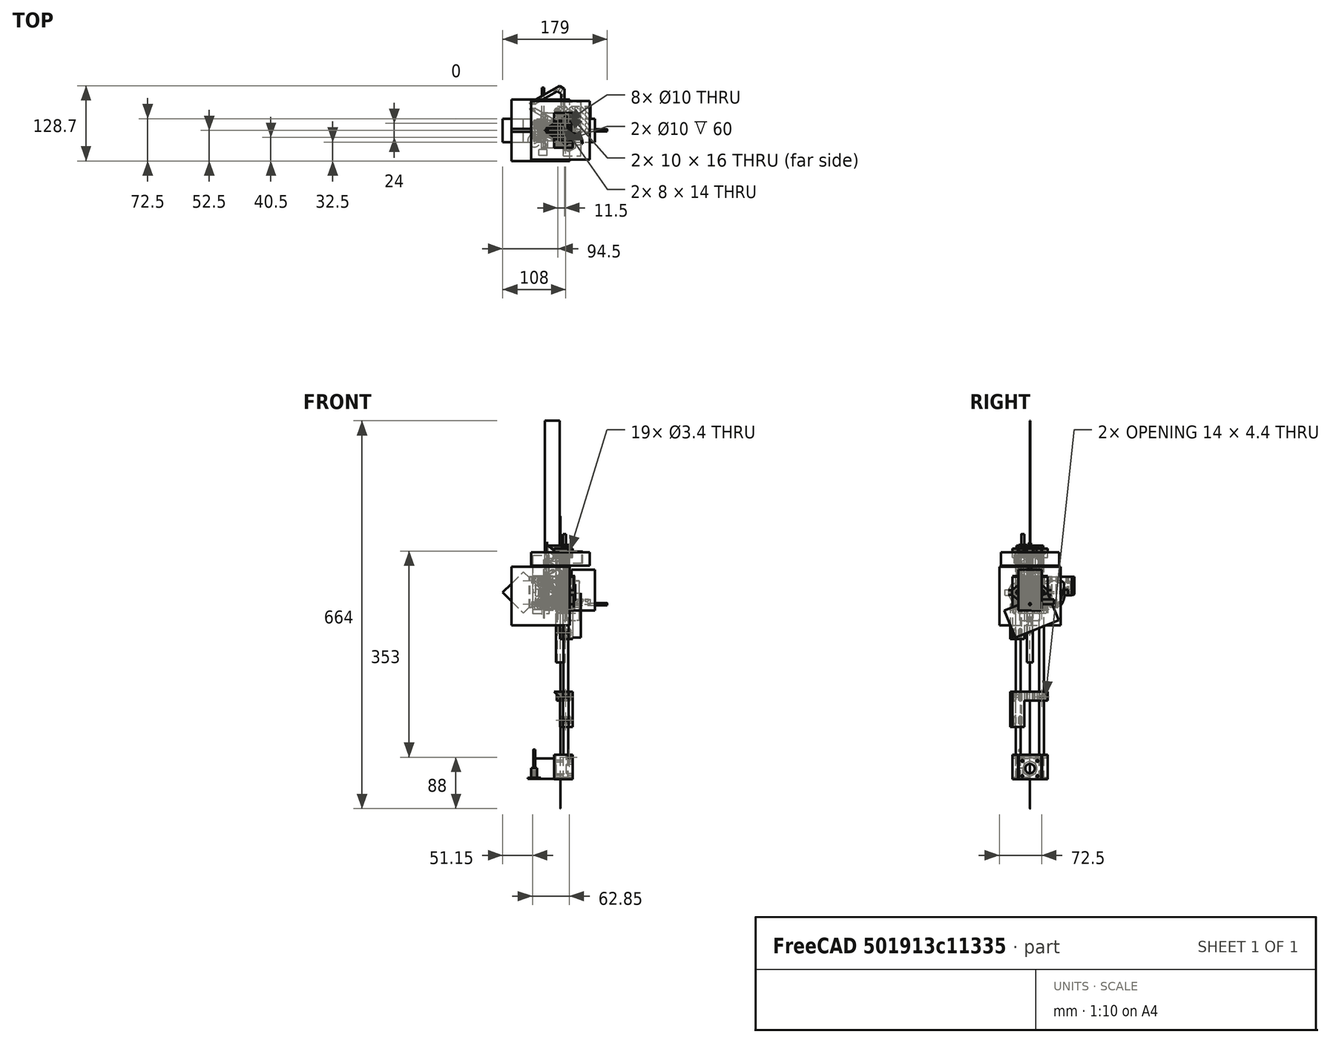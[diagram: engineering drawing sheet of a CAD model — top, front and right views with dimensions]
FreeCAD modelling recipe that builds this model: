
FCSTD DOCUMENT  (FreeCAD 0.16R6703 (Git))
Label: lorenz
License: All rights reserved
LicenseURL: http://en.wikipedia.org/wiki/All_rights_reserved
objects: Part::Cut×262, Part::Box×156, Part::Feature×140, Part::Cylinder×109, Part::Fuse×108, Part::Chamfer×36, Part::MultiCommon×15, Part::Mirroring×10, Part::Cone×10, Part::Sphere×9, App::DocumentObjectGroup×6, Part::Fillet×5
note: 860 computed .brp shape members not serialized (recipe doc carries the construction recipe); baked Part::Feature solids carry a one-line shape summary decoded from their .brp

FEATURE [Part::Box] Box  label="rule"
  Height = 324
  Length = 25.5
  Placement = pos=(-27,-0.33,-10) rot=(0,0,1;0rad)
  Width = 0.66
FEATURE [Part::Cylinder] Cylinder  label="threadrunner1"
  Angle = 360
  Height = 6
  Placement = pos=(-32,3,0) rot=(1,0,0;1.5708rad)
  Radius = 6.5
FEATURE [Part::Cylinder] Cylinder001  label="threadRunner2"
  Angle = 360
  Height = 6
  Placement = pos=(-32,3,40) rot=(1,0,0;1.5708rad)
  Radius = 6.5
FEATURE [Part::Box] Box001  label="Cube"
  Height = 110
  Length = 40
  Placement = pos=(15,-30,-5) rot=(0,0,1;0rad)
  Width = 60
FEATURE [Part::Cylinder] Cylinder002  label="Cylinder"
  Angle = 360
  Height = 100
  Radius = 34
FEATURE [Part::Feature] Box002
  Placement = pos=(18.4808,27.9904,-5) rot=(0,0,1;2.0944rad)
  shape: bbox 71.96 x 64.64 x 110 mm, 6 faces (baked)
FEATURE [Part::Feature] Box003
  Placement = pos=(-33.4808,2.00962,-5) rot=(0,0,1;4.18879rad)
  shape: bbox 71.96 x 64.64 x 110 mm, 6 faces (baked)
FEATURE [Part::Box] Box004  label="Cube001"
  Height = 110
  Length = 40
  Placement = pos=(10,-30,-5) rot=(0,0,1;0rad)
  Width = 60
FEATURE [Part::Feature] Box005
  Placement = pos=(20.9808,23.6603,-5) rot=(0,0,1;2.0944rad)
  shape: bbox 71.96 x 64.64 x 110 mm, 6 faces (baked)
FEATURE [Part::Feature] Box006
  Placement = pos=(-30.9808,6.33975,-5) rot=(0,0,1;4.18879rad)
  shape: bbox 71.96 x 64.64 x 110 mm, 6 faces (baked)
FEATURE [Part::Cylinder] Cylinder003  label="Cylinder001"
  Angle = 360
  Height = 102
  Placement = pos=(0,0,-1) rot=(0,0,1;0rad)
  Radius = 34
FEATURE [Part::Cut] Cut
  Base = -> Cylinder002
  Tool = -> Box001
FEATURE [Part::Cut] Cut001
  Base = -> Cut
  Tool = -> Box002
FEATURE [Part::Cut] Cut002
  Base = -> Cut001
  Tool = -> Box003
FEATURE [Part::Cut] Cut003
  Base = -> Cylinder003
  Tool = -> Box004
FEATURE [Part::Cut] Cut004
  Base = -> Cut003
  Tool = -> Box006
FEATURE [Part::Cut] Cut005
  Base = -> Cut004
  Tool = -> Box005
FEATURE [Part::Cut] Cut006
  Base = -> Cut002
  Tool = -> Cut005
FEATURE [Part::Box] Box007  label="Cube002"
  Height = 110
  Length = 40
  Placement = pos=(40.4808,4.99038,-5) rot=(0,0,1;1.0472rad)
  Width = 60
FEATURE [Part::Feature] Box008
  Placement = pos=(-24.5622,32.5622,-5) rot=(0,0,1;3.14159rad)
  shape: bbox 40 x 60 x 110 mm, 6 faces (baked)
FEATURE [Part::Feature] Box009
  Placement = pos=(-15.9186,-37.5526,-5) rot=(0,0,-1;1.0472rad)
  shape: bbox 71.96 x 64.64 x 110 mm, 6 faces (baked)
FEATURE [Part::Cut] Cut007
  Base = -> Cut006
  Tool = -> Box007
FEATURE [Part::Cut] Cut008
  Base = -> Cut007
  Tool = -> Box008
FEATURE [Part::Cut] Cut009
  Base = -> Cut008
  Tool = -> Box009
FEATURE [Part::Box] Box010  label="Cube003"
  Height = 100
  Length = 37
  Placement = pos=(-22,-4,0) rot=(0,0,1;0rad)
  Width = 8
FEATURE [Part::Box] Box011  label="Cube004"
  Height = 110
  Length = 40
  Placement = pos=(10,-30,-5) rot=(0,0,1;0rad)
  Width = 60
FEATURE [Part::Feature] Box012
  Placement = pos=(20.9808,23.6603,-5) rot=(0,0,1;2.0944rad)
  shape: bbox 71.96 x 64.64 x 110 mm, 6 faces (baked)
FEATURE [Part::Feature] Box013
  Placement = pos=(-30.9808,6.33975,-5) rot=(0,0,1;4.18879rad)
  shape: bbox 71.96 x 64.64 x 110 mm, 6 faces (baked)
FEATURE [Part::Cylinder] Cylinder004  label="Cylinder002"
  Angle = 360
  Height = 102
  Placement = pos=(0,0,-1) rot=(0,0,1;0rad)
  Radius = 34
FEATURE [Part::Cut] Cut010
  Base = -> Cylinder004
  Tool = -> Box011
FEATURE [Part::Cut] Cut011
  Base = -> Cut010
  Tool = -> Box013
FEATURE [Part::Cut] Cut012
  Base = -> Cut011
  Placement = pos=(111,-4.5,71.8801) rot=(-0.250563,-0.935113,0.250563;1.63783rad)
  Tool = -> Box012
FEATURE [Part::Box] Box014  label="Cube005"
  Height = 110
  Length = 40
  Placement = pos=(10,-30,-5) rot=(0,0,1;0rad)
  Width = 60
FEATURE [Part::Feature] Box015
  Placement = pos=(20.9808,23.6603,-5) rot=(0,0,1;2.0944rad)
  shape: bbox 71.96 x 64.64 x 110 mm, 6 faces (baked)
FEATURE [Part::Feature] Box016
  Placement = pos=(-30.9808,6.33975,-5) rot=(0,0,1;4.18879rad)
  shape: bbox 71.96 x 64.64 x 110 mm, 6 faces (baked)
FEATURE [Part::Cylinder] Cylinder005  label="Cylinder003"
  Angle = 360
  Height = 102
  Placement = pos=(0,0,-1) rot=(0,0,1;0rad)
  Radius = 34
FEATURE [Part::Cut] Cut013
  Base = -> Cylinder005
  Tool = -> Box014
FEATURE [Part::Cut] Cut014
  Base = -> Cut013
  Tool = -> Box016
FEATURE [Part::Cut] Cut015
  Base = -> Cut014
  Placement = pos=(111,-4.5,71.8801) rot=(-0.250563,-0.935113,0.250563;1.63783rad)
  Tool = -> Box015
FEATURE [Part::Box] Box017  label="Cube006"
  Height = 29
  Length = 120
  Placement = pos=(0,-18,43) rot=(0,0,1;0rad)
  Width = 36
FEATURE [Part::Box] Box018  label="Cube007"
  Height = 29
  Length = 120
  Placement = pos=(0,-18,43) rot=(0,0,1;0rad)
  Width = 36
FEATURE [Part::Cut] Cut016
  Base = -> Cut012
  Placement = pos=(0,0,-67) rot=(0,0,1;0rad)
  Tool = -> Box017
FEATURE [Part::MultiCommon] Common
  Placement = pos=(8,0,24) rot=(0,0,1;0rad)
  Shapes = -> [Cut015,Box018]
FEATURE [Part::Box] Box019  label="Cube008"
  Height = 110
  Length = 40
  Placement = pos=(10,-30,-5) rot=(0,0,1;0rad)
  Width = 60
FEATURE [Part::Feature] Box020
  Placement = pos=(20.9808,23.6603,-5) rot=(0,0,1;2.0944rad)
  shape: bbox 71.96 x 64.64 x 110 mm, 6 faces (baked)
FEATURE [Part::Feature] Box021
  Placement = pos=(-30.9808,6.33975,-5) rot=(0,0,1;4.18879rad)
  shape: bbox 71.96 x 64.64 x 110 mm, 6 faces (baked)
FEATURE [Part::Cylinder] Cylinder006  label="Cylinder004"
  Angle = 360
  Height = 102
  Placement = pos=(0,0,-1) rot=(0,0,1;0rad)
  Radius = 34
FEATURE [Part::Cut] Cut017
  Base = -> Cylinder006
  Tool = -> Box019
FEATURE [Part::Cut] Cut018
  Base = -> Cut017
  Tool = -> Box021
FEATURE [Part::Cut] Cut019
  Base = -> Cut018
  Placement = pos=(111,4.93525,72.5429) rot=(0.250562,-0.935113,-0.250563;1.63783rad)
  Tool = -> Box020
FEATURE [Part::Box] Box022  label="Cube009"
  Height = 110
  Length = 40
  Placement = pos=(10,-30,-5) rot=(0,0,1;0rad)
  Width = 60
FEATURE [Part::Feature] Box023
  Placement = pos=(20.9808,23.6603,-5) rot=(0,0,1;2.0944rad)
  shape: bbox 71.96 x 64.64 x 110 mm, 6 faces (baked)
FEATURE [Part::Feature] Box024
  Placement = pos=(-30.9808,6.33975,-5) rot=(0,0,1;4.18879rad)
  shape: bbox 71.96 x 64.64 x 110 mm, 6 faces (baked)
FEATURE [Part::Cylinder] Cylinder007  label="Cylinder005"
  Angle = 360
  Height = 102
  Placement = pos=(0,0,-1) rot=(0,0,1;0rad)
  Radius = 34
FEATURE [Part::Cut] Cut020
  Base = -> Cylinder007
  Tool = -> Box022
FEATURE [Part::Cut] Cut021
  Base = -> Cut020
  Tool = -> Box024
FEATURE [Part::Cut] Cut022
  Base = -> Cut021
  Placement = pos=(111,-4.84232,50.4974) rot=(-0.250563,-0.935113,0.250563;1.63783rad)
  Tool = -> Box023
FEATURE [Part::Box] Box025  label="Cube010"
  Height = 110
  Length = 40
  Placement = pos=(10,-30,-5) rot=(0,0,1;0rad)
  Width = 60
FEATURE [Part::Feature] Box026
  Placement = pos=(20.9808,23.6603,-5) rot=(0,0,1;2.0944rad)
  shape: bbox 71.96 x 64.64 x 110 mm, 6 faces (baked)
FEATURE [Part::Feature] Box027
  Placement = pos=(-30.9808,6.33975,-5) rot=(0,0,1;4.18879rad)
  shape: bbox 71.96 x 64.64 x 110 mm, 6 faces (baked)
FEATURE [Part::Cylinder] Cylinder008  label="Cylinder006"
  Angle = 360
  Height = 102
  Placement = pos=(0,0,-1) rot=(0,0,1;0rad)
  Radius = 34
FEATURE [Part::Cut] Cut023
  Base = -> Cylinder008
  Tool = -> Box025
FEATURE [Part::Cut] Cut024
  Base = -> Cut023
  Tool = -> Box027
FEATURE [Part::Cut] Cut025
  Base = -> Cut024
  Placement = pos=(111,4.93525,28.5429) rot=(0.250562,-0.935113,-0.250563;1.63783rad)
  Tool = -> Box026
FEATURE [Part::Fuse] Fusion
  Base = -> Cut016
  Tool = -> Cut025
FEATURE [Part::Fuse] Fusion001
  Base = -> Cut022
  Tool = -> Fusion
FEATURE [Part::Fuse] Fusion002
  Base = -> Cut019
  Tool = -> Fusion001
FEATURE [Part::Fuse] Fusion003
  Base = -> Common
  Placement = pos=(-1,0,0) rot=(0,0,1;0rad)
  Tool = -> Fusion002
FEATURE [Part::Feature] Fusion004
  Placement = pos=(0.5,-0.866025,0) rot=(0,0,1;2.0944rad)
  shape: bbox 77.47 x 103.6 x 91 mm, 26 faces, 5 solids (baked)
FEATURE [Part::Feature] Fusion005
  Placement = pos=(0.5,0.866025,0) rot=(0,0,1;4.18879rad)
  shape: bbox 77.47 x 103.6 x 91 mm, 26 faces, 5 solids (baked)
FEATURE [Part::Cut] Cut026
  Base = -> Cut009
  Tool = -> Fusion003
FEATURE [Part::Cut] Cut027
  Base = -> Cut026
  Tool = -> Fusion004
FEATURE [Part::Cut] Cut028
  Base = -> Cut027
  Tool = -> Fusion005
FEATURE [Part::Fuse] Fusion006
  Base = -> Box010
  Tool = -> Cut028
FEATURE [Part::Box] Box028  label="rule001"
  Height = 324
  Length = 26.5
  Placement = pos=(-27,-0.45,-10) rot=(0,0,1;0rad)
  Width = 0.9
FEATURE [Part::Cut] Cut029  label="stator"
  Base = -> Fusion006
  Tool = -> Box028
FEATURE [Part::Cylinder] Cylinder012
  Angle = 360
  Height = 54
  Placement = pos=(0,0,-7) rot=(0,0,1;0rad)
  Radius = 31
FEATURE [Part::Box] Box029  label="Cube011"
  Height = 60
  Length = 50
  Placement = pos=(21,-25,-10) rot=(0,0,1;0rad)
  Width = 50
FEATURE [Part::Feature] Box030
  Placement = pos=(11.1506,30.6865,-10) rot=(0,0,1;2.0944rad)
  shape: bbox 68.3 x 68.3 x 60 mm, 6 faces (baked)
FEATURE [Part::Feature] Box031
  Placement = pos=(-32.1506,-5.68653,-10) rot=(0,0,1;4.18879rad)
  shape: bbox 68.3 x 68.3 x 60 mm, 6 faces (baked)
FEATURE [Part::Cut] Cut030
  Base = -> Cylinder012
  Tool = -> Box029
FEATURE [Part::Cut] Cut031
  Base = -> Cut030
  Tool = -> Box031
FEATURE [Part::Cut] Cut032
  Base = -> Cut031
  Tool = -> Box030
FEATURE [Part::Box] Box032  label="Cube012"
  Height = 60
  Length = 50
  Placement = pos=(16,-30,-10) rot=(0,0,1;0rad)
  Width = 60
FEATURE [Part::Cylinder] Cylinder013
  Angle = 360
  Height = 56
  Placement = pos=(0,0,-8) rot=(0,0,1;0rad)
  Radius = 31
FEATURE [Part::Feature] Box033
  Placement = pos=(17.9808,28.8564,-10) rot=(0,0,1;2.0944rad)
  shape: bbox 76.96 x 73.3 x 60 mm, 6 faces (baked)
FEATURE [Part::Feature] Box034
  Placement = pos=(-33.9808,1.14359,-10) rot=(0,0,1;4.18879rad)
  shape: bbox 76.96 x 73.3 x 60 mm, 6 faces (baked)
FEATURE [Part::Box] Box035  label="Cube013"
  Height = 60
  Length = 50
  Placement = pos=(-76,-30,-10) rot=(0,0,1;0rad)
  Width = 60
FEATURE [Part::Feature] Box036
  Placement = pos=(63.9808,-50.8179,-10) rot=(0,0,1;2.0944rad)
  shape: bbox 76.96 x 73.3 x 60 mm, 6 faces (baked)
FEATURE [Part::Feature] Box037
  Placement = pos=(12.0192,80.8179,-10) rot=(0,0,1;4.18879rad)
  shape: bbox 76.96 x 73.3 x 60 mm, 6 faces (baked)
FEATURE [Part::Cut] Cut033
  Base = -> Cylinder013
  Tool = -> Box032
FEATURE [Part::Cut] Cut034
  Base = -> Cut033
  Tool = -> Box037
FEATURE [Part::Cut] Cut035
  Base = -> Cut034
  Tool = -> Box036
FEATURE [Part::Cut] Cut036
  Base = -> Cut035
  Tool = -> Box035
FEATURE [Part::Cut] Cut037
  Base = -> Cut036
  Tool = -> Box034
FEATURE [Part::Cut] Cut038
  Base = -> Cut037
  Tool = -> Box033
FEATURE [Part::Cut] Cut039
  Base = -> Cut032
  Tool = -> Cut038
FEATURE [Part::Box] Box038  label="rule002"
  Height = 324
  Length = 26.5
  Placement = pos=(-29,-1.5,-10) rot=(0,0,1;0rad)
  Width = 3
FEATURE [Part::Box] Box039  label="Cube014"
  Height = 15
  Length = 12
  Placement = pos=(-39,-9,-7) rot=(0,0,1;0rad)
  Width = 18
FEATURE [Part::Box] Box040  label="Cube015"
  Height = 15
  Length = 27
  Placement = pos=(-44,-4,-7) rot=(0,0,1;0rad)
  Width = 8
FEATURE [Part::Box] Box041  label="Cube016"
  Height = 15
  Length = 12
  Placement = pos=(-39,-9,32) rot=(0,0,1;0rad)
  Width = 18
FEATURE [Part::Box] Box042  label="Cube017"
  Height = 15
  Length = 27
  Placement = pos=(-44,-4,32) rot=(0,0,1;0rad)
  Width = 8
FEATURE [Part::Fuse] Fusion007
  Base = -> Cut039
  Tool = -> Box039
FEATURE [Part::Fuse] Fusion008
  Base = -> Box041
  Tool = -> Fusion007
FEATURE [Part::Cut] Cut040
  Base = -> Fusion008
  Tool = -> Box042
FEATURE [Part::Cut] Cut041
  Base = -> Cut040
  Tool = -> Box040
FEATURE [Part::Cut] Cut042
  Base = -> Cut041
  Tool = -> Box038
FEATURE [Part::Cylinder] Cylinder014  label="threadrunner002"
  Angle = 360
  Height = 23
  Placement = pos=(-32,11,0) rot=(1,0,0;1.5708rad)
  Radius = 2.2
FEATURE [Part::Cylinder] Cylinder015  label="threadRunner003"
  Angle = 360
  Height = 26
  Placement = pos=(-32,14,40) rot=(1,0,0;1.5708rad)
  Radius = 2.2
FEATURE [Part::Cut] Cut043
  Base = -> Cut042
  Tool = -> Cylinder014
FEATURE [Part::Cut] Cut044
  Base = -> Cut043
  Tool = -> Cylinder015
FEATURE [Part::Cylinder] Cylinder019
  Angle = 360
  Height = 4
  Placement = pos=(-27.5,2,20) rot=(1,0,0;1.5708rad)
  Radius = 5
FEATURE [Part::Cylinder] Cylinder020
  Angle = 360
  Height = 30
  Placement = pos=(-27.5,16,20) rot=(1,0,0;1.5708rad)
  Radius = 1.7
FEATURE [Part::Box] Box043  label="Cube018"
  Height = 12
  Length = 20
  Placement = pos=(-37.5,-2.5,14) rot=(0,0,1;0rad)
  Width = 5
FEATURE [Part::Box] Box044  label="Cube019"
  Height = 12
  Length = 20
  Placement = pos=(-42.5,-12,14) rot=(0,0,1;0rad)
  Width = 5
FEATURE [Part::Box] Box045  label="Cube020"
  Height = 12
  Length = 20
  Placement = pos=(-42.5,7,14) rot=(0,0,1;0rad)
  Width = 5
FEATURE [Part::Box] Box046  label="Cube021"
  Height = 26
  Length = 20
  Placement = pos=(-32.5,-9,0) rot=(0,0,1;0rad)
  Width = 2
FEATURE [Part::Box] Box047  label="Cube022"
  Height = 26
  Length = 20
  Placement = pos=(-32.5,7,0) rot=(0,0,1;0rad)
  Width = 2
FEATURE [Part::Fuse] Fusion009
  Base = -> Cylinder020
  Tool = -> Box043
FEATURE [Part::Fuse] Fusion010
  Base = -> Box047
  Tool = -> Fusion009
FEATURE [Part::Fuse] Fusion011
  Base = -> Box046
  Tool = -> Fusion010
FEATURE [Part::Fuse] Fusion012
  Base = -> Box045
  Tool = -> Fusion011
FEATURE [Part::Fuse] Fusion013
  Base = -> Box044
  Tool = -> Fusion012
FEATURE [Part::Box] Box048  label="Cube023"
  Height = 2
  Length = 25
  Placement = pos=(-34.5,-12,25) rot=(0,0,1;0rad)
  Width = 24
FEATURE [Part::Box] Box049  label="Cube024"
  Height = 15
  Length = 25
  Placement = pos=(-26,-8,0) rot=(0,0,1;0rad)
  Width = 16
FEATURE [Part::Fuse] Fusion014
  Base = -> Fusion013
  Tool = -> Box048
FEATURE [Part::Fuse] Fusion015
  Base = -> Box049
  Tool = -> Fusion014
FEATURE [Part::Box] Box050  label="Cube025"
  Height = 15
  Length = 25
  Placement = pos=(-24,-8,11) rot=(0,0,1;0rad)
  Width = 16
FEATURE [Part::Fuse] Fusion016
  Base = -> Fusion015
  Tool = -> Box050
FEATURE [Part::Feature] Fusion017
  Placement = pos=(0,0,0) rot=(0,0,1;2.0944rad)
  shape: bbox 39.07 x 47.67 x 27 mm, 64 faces (baked)
FEATURE [Part::Feature] Fusion018
  Placement = pos=(0,0,0) rot=(0,0,1;4.18879rad)
  shape: bbox 39.07 x 47.67 x 27 mm, 64 faces (baked)
FEATURE [Part::Cut] Cut045
  Base = -> Cut044
  Tool = -> Fusion017
FEATURE [Part::Cut] Cut046
  Base = -> Cut045
  Tool = -> Fusion018
FEATURE [Part::Feature] Cylinder021
  Placement = pos=(12.0179,-24.8157,20) rot=(0.377964,0.654654,0.654654;2.41886rad)
  shape: bbox 8.464 x 10.66 x 10 mm, 3 faces (baked)
FEATURE [Part::Feature] Cylinder022
  Placement = pos=(15.4821,22.8157,20) rot=(-0.377964,0.654654,0.654654;3.86433rad)
  shape: bbox 8.464 x 10.66 x 10 mm, 3 faces (baked)
FEATURE [Part::Box] Box051  label="Cube026"
  Height = 42
  Length = 15
  Placement = pos=(12,-13,-1) rot=(0,0,1;0rad)
  Width = 26
FEATURE [Part::Box] Box052  label="Cube027"
  Height = 73
  Length = 27
  Placement = pos=(7,-15,-1) rot=(-1,0,0;0.523599rad)
  Width = 5
FEATURE [Part::Cut] Cut047
  Base = -> Box051
  Tool = -> Box052
FEATURE [Part::Feature] Cut048
  Placement = pos=(0,0,0) rot=(0,0,1;2.0944rad)
  shape: bbox 30.02 x 25.99 x 42 mm, 10 faces, 2 solids (baked)
FEATURE [Part::Feature] Cut049
  Placement = pos=(0,0,0) rot=(0,0,1;4.18879rad)
  shape: bbox 30.02 x 25.99 x 42 mm, 10 faces, 2 solids (baked)
FEATURE [Part::Cut] Cut050
  Base = -> Cut046
  Tool = -> Cut047
FEATURE [Part::Cut] Cut051
  Base = -> Cut050
  Tool = -> Cut049
FEATURE [Part::Cut] Cut052
  Base = -> Cut051
  Placement = pos=(0,0,0) rot=(0,0,1;2.0944rad)
  Tool = -> Cut048
FEATURE [Part::Box] Box053  label="Cube028"
  Height = 26
  Length = 10
  Placement = pos=(20,6,0) rot=(0,0,1;0.698132rad)
  Width = 10
FEATURE [Part::Box] Box054  label="Cube029"
  Height = 23
  Length = 6
  Placement = pos=(-2,25,3) rot=(0,0,-1;0.698132rad)
  Width = 7
FEATURE [Part::Feature] Box055
  Placement = pos=(-20.6506,-14.2321,3) rot=(0,0,1;1.39626rad)
  shape: bbox 7.936 x 7.124 x 23 mm, 6 faces (baked)
FEATURE [Part::Feature] Box057
  Placement = pos=(-15.1962,14.3205,0) rot=(0,0,1;2.79253rad)
  shape: bbox 12.82 x 12.82 x 26 mm, 6 faces (baked)
FEATURE [Part::Cut] Cut053
  Base = -> Cut052
  Tool = -> Box053
FEATURE [Part::Cut] Cut054
  Base = -> Cut053
  Tool = -> Box057
FEATURE [Part::Cut] Cut055
  Base = -> Cut054
  Tool = -> Box055
FEATURE [Part::Cut] Cut056  label="slider"
  Base = -> Cut055
  Placement = pos=(0,0,0) rot=(0,0,-1;2.0944rad)
  Tool = -> Box054
FEATURE [Part::Box] Box058  label="Cube030"
  Height = 10
  Length = 3
  Placement = pos=(11,-17,-9) rot=(0,0,1;0rad)
  Width = 34
FEATURE [Part::Box] Box059  label="Cube031"
  Height = 10
  Length = 5
  Placement = pos=(10,2,-20) rot=(1,0,0;0.523599rad)
  Width = 34
FEATURE [Part::Box] Box060  label="Cube032"
  Height = 10
  Length = 5
  Placement = pos=(15,-2,-20) rot=(0,0.258819,0.965926;3.14159rad)
  Width = 34
FEATURE [Part::Cylinder] Cylinder023
  Angle = 360
  Height = 30
  Placement = pos=(13.3,14,-6) rot=(1,0,0;1.5708rad)
  Radius = 1
FEATURE [Part::Fuse] Fusion019
  Base = -> Box058
  Tool = -> Cylinder023
FEATURE [Part::Cut] Cut057
  Base = -> Fusion019
  Tool = -> Box059
FEATURE [Part::Cut] Cut058
  Base = -> Cut057
  Placement = pos=(26,0,0) rot=(0,0,1;3.14159rad)
  Tool = -> Box060
FEATURE [Part::Box] Box061  label="Cube033"
  Height = 10
  Length = 3.4
  Placement = pos=(10.8,-17,-9) rot=(0,0,1;0rad)
  Width = 34
FEATURE [Part::Box] Box062  label="Cube034"
  Height = 10
  Length = 5
  Placement = pos=(10,2,-20.2) rot=(1,0,0;0.523599rad)
  Width = 34
FEATURE [Part::Box] Box063  label="Cube035"
  Height = 10
  Length = 5
  Placement = pos=(15,-2,-20.2) rot=(0,0.258819,0.965926;3.14159rad)
  Width = 34
FEATURE [Part::Cylinder] Cylinder024
  Angle = 360
  Height = 30
  Placement = pos=(13.3,14,-6) rot=(1,0,0;1.5708rad)
  Radius = 1.2
FEATURE [Part::Fuse] Fusion020
  Base = -> Box061
  Tool = -> Cylinder024
FEATURE [Part::Cut] Cut059
  Base = -> Fusion020
  Tool = -> Box062
FEATURE [Part::Cut] Cut060
  Base = -> Cut059
  Placement = pos=(26,0,100) rot=(0,0,1;3.14159rad)
  Tool = -> Box063
FEATURE [Part::Feature] Cut061
  Placement = pos=(-13,22.5167,0) rot=(0,0,-1;1.0472rad)
  shape: bbox 30.94 x 19.6 x 10 mm, 11 faces (baked)
FEATURE [Part::Feature] Cut062
  Placement = pos=(-13,-22.5167,0) rot=(0,0,1;1.0472rad)
  shape: bbox 30.94 x 19.6 x 10 mm, 11 faces (baked)
FEATURE [Part::Feature] Cut063
  Placement = pos=(-13,22.5167,100) rot=(0,0,-1;1.0472rad)
  shape: bbox 31.14 x 19.94 x 10 mm, 11 faces (baked)
FEATURE [Part::Feature] Cut064
  Placement = pos=(-13,-22.5167,100) rot=(0,0,1;1.0472rad)
  shape: bbox 31.14 x 19.94 x 10 mm, 11 faces (baked)
FEATURE [Part::Box] Box064  label="Cube036"
  Height = 110
  Length = 40
  Placement = pos=(10,-30,-5) rot=(0,0,1;0rad)
  Width = 60
FEATURE [Part::Feature] Box065
  Placement = pos=(20.9808,23.6603,-5) rot=(0,0,1;2.0944rad)
  shape: bbox 71.96 x 64.64 x 110 mm, 6 faces (baked)
FEATURE [Part::Feature] Box066
  Placement = pos=(-30.9808,6.33975,-5) rot=(0,0,1;4.18879rad)
  shape: bbox 71.96 x 64.64 x 110 mm, 6 faces (baked)
FEATURE [Part::Cylinder] Cylinder025
  Angle = 360
  Height = 102
  Placement = pos=(0,0,-1) rot=(0,0,1;0rad)
  Radius = 34
FEATURE [Part::Cut] Cut065
  Base = -> Cylinder025
  Tool = -> Box064
FEATURE [Part::Cut] Cut066
  Base = -> Cut065
  Tool = -> Box066
FEATURE [Part::Cut] Cut067
  Base = -> Cut066
  Placement = pos=(111,-4.5,71.8801) rot=(-0.250563,-0.935113,0.250563;1.63783rad)
  Tool = -> Box065
FEATURE [Part::Box] Box067  label="Cube037"
  Height = 29
  Length = 120
  Placement = pos=(0,-18,43) rot=(0,0,1;0rad)
  Width = 36
FEATURE [Part::MultiCommon] Common001
  Placement = pos=(0,0,24) rot=(0,0,1;0rad)
  Shapes = -> [Cut067,Box067]
FEATURE [Part::Box] Box068  label="Cube038"
  Height = 36
  Length = 5
  Placement = pos=(10,-22,66) rot=(0,0,1;0rad)
  Width = 38
FEATURE [Part::MultiCommon] Common002
  Shapes = -> [Common001,Box068]
FEATURE [Part::Feature] Common003
  Placement = pos=(0,0,0) rot=(0,0,1;2.0944rad)
  shape: bbox 28.48 x 19.33 x 17.44 mm, 6 faces (baked)
FEATURE [Part::Feature] Common004
  Placement = pos=(0,0,0) rot=(0,0,1;4.18879rad)
  shape: bbox 28.48 x 19.33 x 17.44 mm, 6 faces (baked)
FEATURE [Part::Fuse] Fusion021
  Base = -> Cut029
  Tool = -> Common003
FEATURE [Part::Fuse] Fusion022
  Base = -> Common004
  Tool = -> Fusion021
FEATURE [Part::Fuse] Fusion023
  Base = -> Cut058
  Tool = -> Fusion022
FEATURE [Part::Fuse] Fusion024
  Base = -> Cut061
  Tool = -> Fusion023
FEATURE [Part::Fuse] Fusion025
  Base = -> Cut062
  Tool = -> Fusion024
FEATURE [Part::Cut] Cut068
  Base = -> Fusion025
  Tool = -> Cut064
FEATURE [Part::Cut] Cut069
  Base = -> Cut068
  Tool = -> Cut063
FEATURE [Part::Cut] Cut070  label="framea"
  Base = -> Cut069
  Tool = -> Cut060
FEATURE [Part::Box] Box069  label="Cube039"
  Height = 110
  Length = 40
  Placement = pos=(15,-30,-5) rot=(0,0,1;0rad)
  Width = 60
FEATURE [Part::Cylinder] Cylinder026  label="Cylinder054060"
  Angle = 360
  Height = 100
  Radius = 34
FEATURE [Part::Feature] Box070
  Placement = pos=(18.4808,27.9904,-5) rot=(0,0,1;2.0944rad)
  shape: bbox 71.96 x 64.64 x 110 mm, 6 faces (baked)
FEATURE [Part::Feature] Box071
  Placement = pos=(-33.4808,2.00962,-5) rot=(0,0,1;4.18879rad)
  shape: bbox 71.96 x 64.64 x 110 mm, 6 faces (baked)
FEATURE [Part::Box] Box072  label="Cube040"
  Height = 110
  Length = 40
  Placement = pos=(10,-30,-5) rot=(0,0,1;0rad)
  Width = 60
FEATURE [Part::Feature] Box073
  Placement = pos=(20.9808,23.6603,-5) rot=(0,0,1;2.0944rad)
  shape: bbox 71.96 x 64.64 x 110 mm, 6 faces (baked)
FEATURE [Part::Feature] Box074
  Placement = pos=(-30.9808,6.33975,-5) rot=(0,0,1;4.18879rad)
  shape: bbox 71.96 x 64.64 x 110 mm, 6 faces (baked)
FEATURE [Part::Cylinder] Cylinder027  label="Cylinder055"
  Angle = 360
  Height = 102
  Placement = pos=(0,0,-1) rot=(0,0,1;0rad)
  Radius = 34
FEATURE [Part::Cut] Cut071
  Base = -> Cylinder026
  Tool = -> Box069
FEATURE [Part::Cut] Cut072
  Base = -> Cut071
  Tool = -> Box070
FEATURE [Part::Cut] Cut073
  Base = -> Cut072
  Tool = -> Box071
FEATURE [Part::Cut] Cut074
  Base = -> Cylinder027
  Tool = -> Box072
FEATURE [Part::Cut] Cut075
  Base = -> Cut074
  Tool = -> Box074
FEATURE [Part::Cut] Cut076
  Base = -> Cut075
  Tool = -> Box073
FEATURE [Part::Cut] Cut077
  Base = -> Cut073
  Tool = -> Cut076
FEATURE [Part::Box] Box075  label="Cube041"
  Height = 110
  Length = 40
  Placement = pos=(40.4808,4.99038,-5) rot=(0,0,1;1.0472rad)
  Width = 60
FEATURE [Part::Feature] Box076
  Placement = pos=(-24.5622,32.5622,-5) rot=(0,0,1;3.14159rad)
  shape: bbox 40 x 60 x 110 mm, 6 faces (baked)
FEATURE [Part::Feature] Box077
  Placement = pos=(-15.9186,-37.5526,-5) rot=(0,0,-1;1.0472rad)
  shape: bbox 71.96 x 64.64 x 110 mm, 6 faces (baked)
FEATURE [Part::Cut] Cut078
  Base = -> Cut077
  Tool = -> Box075
FEATURE [Part::Cut] Cut079
  Base = -> Cut078
  Tool = -> Box076
FEATURE [Part::Cut] Cut080
  Base = -> Cut079
  Tool = -> Box077
FEATURE [Part::Box] Box078  label="Cube042"
  Height = 100
  Length = 37
  Placement = pos=(-22,-4,0) rot=(0,0,1;0rad)
  Width = 8
FEATURE [Part::Box] Box079  label="Cube043"
  Height = 110
  Length = 40
  Placement = pos=(10,-30,-5) rot=(0,0,1;0rad)
  Width = 60
FEATURE [Part::Feature] Box080
  Placement = pos=(20.9808,23.6603,-5) rot=(0,0,1;2.0944rad)
  shape: bbox 71.96 x 64.64 x 110 mm, 6 faces (baked)
FEATURE [Part::Feature] Box081
  Placement = pos=(-30.9808,6.33975,-5) rot=(0,0,1;4.18879rad)
  shape: bbox 71.96 x 64.64 x 110 mm, 6 faces (baked)
FEATURE [Part::Cylinder] Cylinder028  label="Cylinder026"
  Angle = 360
  Height = 102
  Placement = pos=(0,0,-1) rot=(0,0,1;0rad)
  Radius = 34
FEATURE [Part::Cut] Cut081
  Base = -> Cylinder028
  Tool = -> Box079
FEATURE [Part::Cut] Cut082
  Base = -> Cut081
  Tool = -> Box081
FEATURE [Part::Cut] Cut083
  Base = -> Cut082
  Placement = pos=(111,-4.5,71.8801) rot=(-0.250563,-0.935113,0.250563;1.63783rad)
  Tool = -> Box080
FEATURE [Part::Box] Box082  label="Cube044"
  Height = 110
  Length = 40
  Placement = pos=(10,-30,-5) rot=(0,0,1;0rad)
  Width = 60
FEATURE [Part::Feature] Box083
  Placement = pos=(20.9808,23.6603,-5) rot=(0,0,1;2.0944rad)
  shape: bbox 71.96 x 64.64 x 110 mm, 6 faces (baked)
FEATURE [Part::Feature] Box084
  Placement = pos=(-30.9808,6.33975,-5) rot=(0,0,1;4.18879rad)
  shape: bbox 71.96 x 64.64 x 110 mm, 6 faces (baked)
FEATURE [Part::Cylinder] Cylinder029  label="Cylinder027"
  Angle = 360
  Height = 102
  Placement = pos=(0,0,-1) rot=(0,0,1;0rad)
  Radius = 34
FEATURE [Part::Cut] Cut084
  Base = -> Cylinder029
  Tool = -> Box082
FEATURE [Part::Cut] Cut085
  Base = -> Cut084
  Tool = -> Box084
FEATURE [Part::Cut] Cut086
  Base = -> Cut085
  Placement = pos=(111,-4.5,71.8801) rot=(-0.250563,-0.935113,0.250563;1.63783rad)
  Tool = -> Box083
FEATURE [Part::Box] Box085  label="Cube045"
  Height = 29
  Length = 120
  Placement = pos=(0,-18,43) rot=(0,0,1;0rad)
  Width = 36
FEATURE [Part::Box] Box086  label="Cube046"
  Height = 29
  Length = 120
  Placement = pos=(0,-18,43) rot=(0,0,1;0rad)
  Width = 36
FEATURE [Part::Cut] Cut087
  Base = -> Cut083
  Placement = pos=(0,0,-67) rot=(0,0,1;0rad)
  Tool = -> Box085
FEATURE [Part::MultiCommon] Common005
  Placement = pos=(8,0,24) rot=(0,0,1;0rad)
  Shapes = -> [Cut086,Box086]
FEATURE [Part::Box] Box087  label="Cube047"
  Height = 110
  Length = 40
  Placement = pos=(10,-30,-5) rot=(0,0,1;0rad)
  Width = 60
FEATURE [Part::Feature] Box088
  Placement = pos=(20.9808,23.6603,-5) rot=(0,0,1;2.0944rad)
  shape: bbox 71.96 x 64.64 x 110 mm, 6 faces (baked)
FEATURE [Part::Feature] Box089
  Placement = pos=(-30.9808,6.33975,-5) rot=(0,0,1;4.18879rad)
  shape: bbox 71.96 x 64.64 x 110 mm, 6 faces (baked)
FEATURE [Part::Cylinder] Cylinder030  label="Cylinder028"
  Angle = 360
  Height = 102
  Placement = pos=(0,0,-1) rot=(0,0,1;0rad)
  Radius = 34
FEATURE [Part::Cut] Cut088
  Base = -> Cylinder030
  Tool = -> Box087
FEATURE [Part::Cut] Cut089
  Base = -> Cut088
  Tool = -> Box089
FEATURE [Part::Cut] Cut090
  Base = -> Cut089
  Placement = pos=(111,4.93525,72.5429) rot=(0.250562,-0.935113,-0.250563;1.63783rad)
  Tool = -> Box088
FEATURE [Part::Box] Box090  label="Cube048"
  Height = 110
  Length = 40
  Placement = pos=(10,-30,-5) rot=(0,0,1;0rad)
  Width = 60
FEATURE [Part::Feature] Box091
  Placement = pos=(20.9808,23.6603,-5) rot=(0,0,1;2.0944rad)
  shape: bbox 71.96 x 64.64 x 110 mm, 6 faces (baked)
FEATURE [Part::Feature] Box092
  Placement = pos=(-30.9808,6.33975,-5) rot=(0,0,1;4.18879rad)
  shape: bbox 71.96 x 64.64 x 110 mm, 6 faces (baked)
FEATURE [Part::Cylinder] Cylinder031  label="Cylinder029"
  Angle = 360
  Height = 102
  Placement = pos=(0,0,-1) rot=(0,0,1;0rad)
  Radius = 34
FEATURE [Part::Cut] Cut091
  Base = -> Cylinder031
  Tool = -> Box090
FEATURE [Part::Cut] Cut092
  Base = -> Cut091
  Tool = -> Box092
FEATURE [Part::Cut] Cut093
  Base = -> Cut092
  Placement = pos=(111,-4.84232,50.4974) rot=(-0.250563,-0.935113,0.250563;1.63783rad)
  Tool = -> Box091
FEATURE [Part::Box] Box093  label="Cube049"
  Height = 110
  Length = 40
  Placement = pos=(10,-30,-5) rot=(0,0,1;0rad)
  Width = 60
FEATURE [Part::Feature] Box094
  Placement = pos=(20.9808,23.6603,-5) rot=(0,0,1;2.0944rad)
  shape: bbox 71.96 x 64.64 x 110 mm, 6 faces (baked)
FEATURE [Part::Feature] Box095
  Placement = pos=(-30.9808,6.33975,-5) rot=(0,0,1;4.18879rad)
  shape: bbox 71.96 x 64.64 x 110 mm, 6 faces (baked)
FEATURE [Part::Cylinder] Cylinder032  label="Cylinder030"
  Angle = 360
  Height = 102
  Placement = pos=(0,0,-1) rot=(0,0,1;0rad)
  Radius = 34
FEATURE [Part::Cut] Cut094
  Base = -> Cylinder032
  Tool = -> Box093
FEATURE [Part::Cut] Cut095
  Base = -> Cut094
  Tool = -> Box095
FEATURE [Part::Cut] Cut096
  Base = -> Cut095
  Placement = pos=(111,4.93525,28.5429) rot=(0.250562,-0.935113,-0.250563;1.63783rad)
  Tool = -> Box094
FEATURE [Part::Fuse] Fusion026
  Base = -> Cut087
  Tool = -> Cut096
FEATURE [Part::Fuse] Fusion027
  Base = -> Cut093
  Tool = -> Fusion026
FEATURE [Part::Fuse] Fusion028
  Base = -> Cut090
  Tool = -> Fusion027
FEATURE [Part::Fuse] Fusion029
  Base = -> Common005
  Placement = pos=(-1,0,0) rot=(0,0,1;0rad)
  Tool = -> Fusion028
FEATURE [Part::Feature] Fusion030
  Placement = pos=(0.5,-0.866025,0) rot=(0,0,1;2.0944rad)
  shape: bbox 77.47 x 103.6 x 91 mm, 26 faces, 5 solids (baked)
FEATURE [Part::Feature] Fusion031
  Placement = pos=(0.5,0.866025,0) rot=(0,0,1;4.18879rad)
  shape: bbox 77.47 x 103.6 x 91 mm, 26 faces, 5 solids (baked)
FEATURE [Part::Cut] Cut097
  Base = -> Cut080
  Tool = -> Fusion029
FEATURE [Part::Cut] Cut098
  Base = -> Cut097
  Tool = -> Fusion030
FEATURE [Part::Cut] Cut099
  Base = -> Cut098
  Tool = -> Fusion031
FEATURE [Part::Fuse] Fusion032
  Base = -> Box078
  Tool = -> Cut099
FEATURE [Part::Box] Box096  label="rule003"
  Height = 324
  Length = 26.5
  Placement = pos=(-27,-0.45,-10) rot=(0,0,1;0rad)
  Width = 0.9
FEATURE [Part::Cut] Cut100  label="stator001"
  Base = -> Fusion032
  Tool = -> Box096
FEATURE [Part::Box] Box097  label="Cube050"
  Height = 10
  Length = 3
  Placement = pos=(11,-17,-9) rot=(0,0,1;0rad)
  Width = 34
FEATURE [Part::Box] Box098  label="Cube051"
  Height = 10
  Length = 5
  Placement = pos=(10,2,-20) rot=(1,0,0;0.523599rad)
  Width = 34
FEATURE [Part::Box] Box099  label="Cube052"
  Height = 10
  Length = 5
  Placement = pos=(15,-2,-20) rot=(0,0.258819,0.965926;3.14159rad)
  Width = 34
FEATURE [Part::Cylinder] Cylinder033
  Angle = 360
  Height = 30
  Placement = pos=(13.5,14,-6) rot=(1,0,0;1.5708rad)
  Radius = 1.2
FEATURE [Part::Fuse] Fusion033
  Base = -> Box097
  Tool = -> Cylinder033
FEATURE [Part::Cut] Cut101
  Base = -> Fusion033
  Tool = -> Box098
FEATURE [Part::Cut] Cut102
  Base = -> Cut101
  Placement = pos=(26,0,0) rot=(0,0,1;3.14159rad)
  Tool = -> Box099
FEATURE [Part::Box] Box100  label="Cube053"
  Height = 10
  Length = 3.4
  Placement = pos=(10.8,-17,-9) rot=(0,0,1;0rad)
  Width = 34
FEATURE [Part::Box] Box101  label="Cube054"
  Height = 10
  Length = 5
  Placement = pos=(10,2,-20.2) rot=(1,0,0;0.523599rad)
  Width = 34
FEATURE [Part::Box] Box102  label="Cube055"
  Height = 10
  Length = 5
  Placement = pos=(15,-2,-20.2) rot=(0,0.258819,0.965926;3.14159rad)
  Width = 34
FEATURE [Part::Cylinder] Cylinder034
  Angle = 360
  Height = 30
  Placement = pos=(13.5,14,-6) rot=(1,0,0;1.5708rad)
  Radius = 1.1
FEATURE [Part::Fuse] Fusion034
  Base = -> Box100
  Tool = -> Cylinder034
FEATURE [Part::Cut] Cut103
  Base = -> Fusion034
  Tool = -> Box101
FEATURE [Part::Cut] Cut104
  Base = -> Cut103
  Placement = pos=(26,0,100) rot=(0,0,1;3.14159rad)
  Tool = -> Box102
FEATURE [Part::Feature] Common006
  Placement = pos=(0,0,0) rot=(0,0,1;2.0944rad)
  shape: bbox 28.48 x 19.33 x 17.44 mm, 6 faces (baked)
FEATURE [Part::Feature] Common007
  Placement = pos=(0,0,0) rot=(0,0,1;4.18879rad)
  shape: bbox 28.48 x 19.33 x 17.44 mm, 6 faces (baked)
FEATURE [Part::Fuse] Fusion035
  Base = -> Cut100
  Tool = -> Common006
FEATURE [Part::Fuse] Fusion036
  Base = -> Common007
  Tool = -> Fusion035
FEATURE [Part::Feature] Cut105
  Placement = pos=(-13,22.5167,0) rot=(0,0,-1;1.0472rad)
  shape: bbox 30.94 x 19.6 x 10 mm, 11 faces (baked)
FEATURE [Part::Feature] Cut106
  Placement = pos=(-13,-22.5167,0) rot=(0,0,1;1.0472rad)
  shape: bbox 30.94 x 19.6 x 10 mm, 11 faces (baked)
FEATURE [Part::Feature] Cut107
  Placement = pos=(-13,22.5167,100) rot=(0,0,-1;1.0472rad)
  shape: bbox 31.14 x 19.94 x 10 mm, 11 faces (baked)
FEATURE [Part::Feature] Cut108
  Placement = pos=(-13,-22.5167,100) rot=(0,0,1;1.0472rad)
  shape: bbox 31.14 x 19.94 x 10 mm, 11 faces (baked)
FEATURE [Part::Fuse] Fusion037
  Base = -> Fusion036
  Tool = -> Cut105
FEATURE [Part::Fuse] Fusion038
  Base = -> Cut106
  Tool = -> Fusion037
FEATURE [Part::Fuse] Fusion039
  Base = -> Cut102
  Tool = -> Fusion038
FEATURE [Part::Cut] Cut109
  Base = -> Fusion039
  Tool = -> Cut108
FEATURE [Part::Cut] Cut110
  Base = -> Cut109
  Tool = -> Cut107
FEATURE [Part::Cut] Cut111  label="frame"
  Base = -> Cut110
  Tool = -> Cut104
FEATURE [Part::Cylinder] Cylinder035  label="roller"
  Angle = 360
  Height = 4
  Placement = pos=(-28.5,2,20) rot=(1,0,0;1.5708rad)
  Radius = 5
FEATURE [Part::Feature] Cylinder036  label="roller1"
  Placement = pos=(12.5179,-25.6817,20) rot=(0.377964,0.654654,0.654654;2.41886rad)
  shape: bbox 8.464 x 10.66 x 10 mm, 3 faces (baked)
FEATURE [Part::Feature] Cylinder037  label="roller2"
  Placement = pos=(15.9821,23.6817,20) rot=(-0.377964,0.654654,0.654654;3.86433rad)
  shape: bbox 8.464 x 10.66 x 10 mm, 3 faces (baked)
FEATURE [Part::Box] Box103  label="Cube056"
  Height = 32
  Length = 10
  Placement = pos=(13,-30,15) rot=(0,0,1;0rad)
  Width = 60
FEATURE [Part::Cylinder] Cylinder039  label="M3"
  Angle = 360
  Height = 56
  Placement = pos=(-28.5,27,20) rot=(1,0,0;1.5708rad)
  Radius = 1.7
FEATURE [Part::Feature] Cylinder040  label="Cylinder040xxx"
  Placement = pos=(-9.13269,-38.1817,-11) rot=(0.377964,0.654654,0.654654;2.41885rad)
  shape: bbox 50.2 x 30.94 x 3.4 mm, 3 faces (baked)
FEATURE [Part::Box] Box104  label="Cube057"
  Height = 100
  Length = 100
  Placement = pos=(-84,-2.5,-36) rot=(0,0,1;0rad)
  Width = 55
FEATURE [Part::Box] Box105  label="Cube058"
  Height = 100
  Length = 100
  Placement = pos=(-84,-52.5,-36) rot=(0,0,1;0rad)
  Width = 55
FEATURE [Part::Box] Box106  label="Cube059"
  Height = 34
  Length = 6
  Placement = pos=(11,-21,14) rot=(0,0,1;0rad)
  Width = 42
FEATURE [Part::Feature] Box108
  Placement = pos=(-3.46633,98.9961,-36) rot=(0,0,1;4.18879rad)
  shape: bbox 97.63 x 114.1 x 100 mm, 6 faces (baked)
FEATURE [Part::Cut] Cut112
  Base = -> Box103
  Tool = -> Box108
FEATURE [Part::Feature] Box109
  Placement = pos=(44.1651,-71.4961,-36) rot=(0,0,1;2.0944rad)
  shape: bbox 97.63 x 114.1 x 100 mm, 6 faces (baked)
FEATURE [Part::Cut] Cut113
  Base = -> Cut112
  Tool = -> Box109
FEATURE [Part::Cut] Cut114
  Base = -> Cut113
  Tool = -> Box106
FEATURE [Part::Box] Box110  label="Cube060"
  Height = 53
  Length = 10
  Placement = pos=(13,-30,-6) rot=(0,0,1;0rad)
  Width = 60
FEATURE [Part::Box] Box111  label="Cube061"
  Height = 55
  Length = 6
  Placement = pos=(11,-21,-7) rot=(0,0,1;0rad)
  Width = 42
FEATURE [Part::Box] Box112  label="Cube062"
  Height = 10
  Length = 10
  Placement = pos=(-34,8,15) rot=(0,0,1;0rad)
  Width = 10
FEATURE [Part::Feature] Box112002
  Placement = pos=(23.9282,25.4449,15) rot=(0,0,1;4.18879rad)
  shape: bbox 13.66 x 13.66 x 10 mm, 6 faces (baked)
FEATURE [Part::Cut] Cut115
  Base = -> Cut114
  Tool = -> Box112002
FEATURE [Part::Box] Box112003  label="Cube063"
  Height = 10
  Length = 10
  Placement = pos=(-34,-18,15) rot=(0,0,1;0rad)
  Width = 10
FEATURE [Part::Feature] Box112004
  Placement = pos=(32.5885,-20.4449,15) rot=(0,0,1;2.0944rad)
  shape: bbox 13.66 x 13.66 x 10 mm, 6 faces (baked)
FEATURE [Part::Cut] Cut116
  Base = -> Cut115
  Tool = -> Box112004
FEATURE [Part::Box] Box112005  label="Cube064"
  Height = 34
  Length = 12
  Placement = pos=(14,-17,6) rot=(0,0,1;0rad)
  Width = 34
FEATURE [Part::Cut] Cut117
  Base = -> Cut116
  Tool = -> Box112005
FEATURE [Part::Fillet] Fillet
  Base = -> Cut117
  Edges = 1 edges r=6: [Edge41]
FEATURE [Part::Fillet] Fillet001
  Base = -> Fillet
  Edges = 1 edges r=6: [Edge23]
FEATURE [Part::Feature] Cylinder042  label="Cylinder056xxx"
  Placement = pos=(-9.13269,-38.1817,-11) rot=(0.377964,0.654654,0.654654;2.41885rad)
  shape: bbox 50.2 x 30.94 x 3.4 mm, 3 faces (baked)
FEATURE [Part::Feature] Cylinder043  label="Cylinder057xxx"
  Placement = pos=(37.6327,11.1817,-11) rot=(-0.377964,0.654654,0.654654;3.86433rad)
  shape: bbox 50.2 x 30.94 x 3.4 mm, 3 faces (baked)
FEATURE [Part::Cut] Cut118
  Base = -> Fillet001
  Tool = -> Cylinder042
FEATURE [Part::Cut] Cut119  label="idler-carriage-1"
  Base = -> Cut118
  Tool = -> Cylinder043
FEATURE [Part::Feature] Box112007
  Placement = pos=(-32.4808,3.74167,-6) rot=(0,0,1;4.18879rad)
  shape: bbox 56.96 x 38.66 x 53 mm, 6 faces (baked)
FEATURE [Part::Feature] Box112009
  Placement = pos=(-23.6865,0.973721,-7) rot=(0,0,1;4.18879rad)
  shape: bbox 39.37 x 26.2 x 55 mm, 6 faces (baked)
FEATURE [Part::Feature] Box112010
  Placement = pos=(87.4663,-46.4961,-36) rot=(0,0,1;2.0944rad)
  shape: bbox 97.63 x 114.1 x 100 mm, 6 faces (baked)
FEATURE [Part::Cut] Cut120
  Base = -> Box112007
  Tool = -> Box112010
FEATURE [Part::Cut] Cut121
  Base = -> Cut120
  Tool = -> Box112009
FEATURE [Part::Cut] Cut122
  Base = -> Cut121
  Tool = -> Cylinder040
FEATURE [Part::Feature] Box112011
  Placement = pos=(10.0718,-33.4449,15) rot=(0,0,1;2.0944rad)
  shape: bbox 13.66 x 13.66 x 10 mm, 6 faces (baked)
FEATURE [Part::Cut] Cut123
  Base = -> Cut122
  Tool = -> Box112011
FEATURE [Part::Box] Box112012  label="Cube065"
  Height = 100
  Length = 100
  Placement = pos=(-84,-3.5,-36) rot=(0,0,1;0rad)
  Width = 55
FEATURE [Part::Cut] Cut124
  Base = -> Cut123
  Tool = -> Box112012
FEATURE [Part::Cylinder] Cylinder044  label="threadrunner003"
  Angle = 360
  Height = 41
  Placement = pos=(-32,15,0) rot=(1,0,0;1.5708rad)
  Radius = 1.7
FEATURE [Part::Cylinder] Cylinder045  label="threadRunner004"
  Angle = 360
  Height = 38
  Placement = pos=(-32,17,40) rot=(1,0,0;1.5708rad)
  Radius = 1.7
FEATURE [Part::Box] Box112013  label="Cube066"
  Height = 10
  Length = 10
  Placement = pos=(-38,-17,-6) rot=(0,0,1;0rad)
  Width = 10
FEATURE [Part::Box] Box112014  label="Cube067"
  Height = 11
  Length = 10
  Placement = pos=(-38,-17,36) rot=(0,0,1;0rad)
  Width = 10
FEATURE [Part::Cut] Cut125
  Base = -> Cut124
  Tool = -> Box112013
FEATURE [Part::Cut] Cut126
  Base = -> Cut125
  Tool = -> Box112014
FEATURE [Part::Cut] Cut127
  Base = -> Cut126
  Tool = -> Cylinder045
FEATURE [Part::Cut] Cut128
  Base = -> Cut127
  Tool = -> Cylinder044
FEATURE [Part::Cylinder] Cylinder046  label="roller003"
  Angle = 360
  Height = 4
  Placement = pos=(-28.5,2,40) rot=(1,0,0;1.5708rad)
  Radius = 5
FEATURE [Part::Box] Box112015  label="Cube068"
  Height = 11
  Length = 10
  Placement = pos=(-37,-4.5,36) rot=(0,0,1;0rad)
  Width = 9
FEATURE [Part::Box] Box112017  label="Cube069"
  Height = 11
  Length = 10
  Placement = pos=(-37,-14,36) rot=(0,0,1;0rad)
  Width = 8
FEATURE [Part::Box] Box112019  label="Cube070"
  Height = 11
  Length = 10
  Placement = pos=(-37,6,36) rot=(0,0,1;0rad)
  Width = 8
FEATURE [Part::Cylinder] Cylinder047  label="threadRunner005"
  Angle = 360
  Height = 38
  Placement = pos=(-32,17,40) rot=(1,0,0;1.5708rad)
  Radius = 1.7
FEATURE [Part::Box] Box112022  label="Cube071"
  Height = 11
  Length = 10
  Placement = pos=(-37,6,36) rot=(0,0,1;0rad)
  Width = 8
FEATURE [Part::Feature] Box112015001
  Placement = pos=(22.3971,-29.7929,36) rot=(0,0,1;2.0944rad)
  shape: bbox 12.79 x 13.16 x 11 mm, 6 faces (baked)
FEATURE [Part::Fuse] Fusion040
  Base = -> Cut128
  Tool = -> Box112015001
FEATURE [Part::Box] Box112015002  label="Cube072"
  Height = 50
  Length = 30
  Placement = pos=(5,-25,-57) rot=(1,0,0;0.383972rad)
  Width = 80
FEATURE [Part::Feature] Box112015002002
  Placement = pos=(-24.1506,8.16987,-59) rot=(-0.109501,0.189662,0.975724;4.16764rad)
  shape: bbox 95.46 x 72.43 x 76.33 mm, 6 faces (baked)
FEATURE [Part::Cut] Cut129
  Base = -> Fusion040
  Tool = -> Box112015002002
FEATURE [Part::Box] Box112015002003  label="Cube073"
  Height = 55
  Length = 21
  Placement = pos=(11,-17,-15) rot=(0,0,1;0rad)
  Width = 34
FEATURE [Part::Box] Box112015002004  label="Cube074"
  Height = 80
  Length = 23
  Placement = pos=(10,-55,0) rot=(-1,0,0;0.628319rad)
  Width = 34
FEATURE [Part::Cut] Cut130
  Base = -> Box112015002003
  Tool = -> Box112015002004
FEATURE [Part::Box] Box112015002005  label="Cube075"
  Height = 80
  Length = 21
  Placement = pos=(11,-17,-38) rot=(0,0,1;0rad)
  Width = 34
FEATURE [Part::Box] Box112015002006  label="Cube076"
  Height = 80
  Length = 23
  Placement = pos=(10,-48,-6) rot=(-1,0,0;0.506145rad)
  Width = 34
FEATURE [Part::Cut] Cut131
  Base = -> Box112015002005
  Tool = -> Box112015002006
FEATURE [Part::Fillet] Fillet002
  Base = -> Cut131
  Edges = 1 edges r=4: [Edge9]
  Placement = pos=(0,0,10) rot=(0,0,1;0rad)
FEATURE [Part::Feature] Fillet004
  Placement = pos=(0,0,10) rot=(0,0,1;4.18879rad)
  shape: bbox 39.94 x 35.19 x 67.67 mm, 7 faces (baked)
FEATURE [Part::Cut] Cut132
  Base = -> Cut129
  Tool = -> Fillet004
FEATURE [Part::Box] Box112015002007  label="Cube077"
  Height = 10
  Length = 28
  Placement = pos=(-2,-39,6) rot=(0,0,1;0rad)
  Width = 24
FEATURE [Part::Cut] Cut133
  Base = -> Cut132
  Tool = -> Box112015002007
FEATURE [Part::Fillet] Fillet005
  Base = -> Cut133
  Edges = 1 edges r=20: [Edge73]
FEATURE [Part::Mirroring] Part__Mirroring  label="Fillet005 (Mirror #1)"
  Base = (0,0,0)
  Normal = (0,1,0)
  Source = -> Fillet005
FEATURE [Part::Fillet] Fillet006
  Base = -> Cut133
  Edges = 1 edges r=20: [Edge73]
FEATURE [Part::Fuse] Fusion041
  Base = -> Cut119
  Tool = -> Part__Mirroring
FEATURE [Part::Fuse] Fusion042  label="idler-carriage"
  Base = -> Fillet006
  Placement = pos=(-15.8497,41.2794,-4.15018e-05) rot=(0,0,1;0rad)
  Tool = -> Fusion041
FEATURE [Part::Cylinder] Cylinder048  label="Cylinder058"
  Angle = 360
  Height = 100
  Radius = 34
FEATURE [Part::Box] Box112015002008  label="Cube078"
  Height = 110
  Length = 40
  Placement = pos=(15,-30,-5) rot=(0,0,1;0rad)
  Width = 60
FEATURE [Part::Box] Box112015002009  label="Cube079"
  Height = 110
  Length = 40
  Placement = pos=(40.4808,4.99038,-5) rot=(0,0,1;1.0472rad)
  Width = 60
FEATURE [Part::Box] Box112015002010  label="rule004"
  Height = 324
  Length = 25.5
  Placement = pos=(-27,-0.45,-10) rot=(0,0,1;0rad)
  Width = 0.9
FEATURE [Part::Feature] Box112015002011
  Placement = pos=(18.4808,27.9904,-5) rot=(0,0,1;2.0944rad)
  shape: bbox 71.96 x 64.64 x 110 mm, 6 faces (baked)
FEATURE [Part::Feature] Box112015002012
  Placement = pos=(-33.4808,2.00962,-5) rot=(0,0,1;4.18879rad)
  shape: bbox 71.96 x 64.64 x 110 mm, 6 faces (baked)
FEATURE [Part::Feature] Box112015002013
  Placement = pos=(-24.5622,32.5622,-5) rot=(0,0,1;3.14159rad)
  shape: bbox 40 x 60 x 110 mm, 6 faces (baked)
FEATURE [Part::Feature] Box112015002014
  Placement = pos=(-15.9186,-37.5526,-5) rot=(0,0,-1;1.0472rad)
  shape: bbox 71.96 x 64.64 x 110 mm, 6 faces (baked)
FEATURE [Part::Cylinder] Cylinder049  label="Cylinder059"
  Angle = 360
  Height = 130
  Placement = pos=(7,0,-10) rot=(0,0,1;0rad)
  Radius = 2.5
FEATURE [Part::Cylinder] Cylinder050  label="Cylinder060"
  Angle = 360
  Height = 16
  Placement = pos=(7,0,-1) rot=(0,0,1;0rad)
  Radius = 5
FEATURE [Part::Cylinder] Cylinder051  label="Cylinder061"
  Angle = 360
  Height = 16
  Placement = pos=(7,0,85) rot=(0,0,1;0rad)
  Radius = 5
FEATURE [Part::Cylinder] Cylinder052  label="Cylinder062"
  Angle = 360
  Height = 28
  Radius = 4.8
FEATURE [Part::Cylinder] Cylinder053  label="Cylinder063"
  Angle = 360
  Height = 50
  Placement = pos=(0,0,-4) rot=(0,0,1;0rad)
  Radius = 2.5
FEATURE [Part::Cut] Cut144  label="locating-cylinder-1"
  Base = -> Cylinder052
  Placement = pos=(-6,33,0) rot=(0,0,1;0rad)
  Tool = -> Cylinder053
FEATURE [Part::Cylinder] Cylinder054  label="PTFE-tube"
  Angle = 360
  Height = 110
  Placement = pos=(-23,0,-5) rot=(0,0,1;0rad)
  Radius = 2
FEATURE [Part::Cone] Cone
  Angle = 360
  Height = 2.5
  Placement = pos=(7,0,15) rot=(0,0,1;0rad)
  Radius1 = 5
  Radius2 = 2.5
FEATURE [Part::Cylinder] Cylinder054003  label="v-bearing-1"
  Angle = 360
  Height = 7
  Placement = pos=(-31.9,3.5,0) rot=(1,0,0;1.5708rad)
  Radius = 8
FEATURE [Part::Cylinder] Cylinder054005
  Angle = 360
  Height = 7
  Placement = pos=(-30,3.5,20) rot=(1,0,0;1.5708rad)
  Radius = 7
FEATURE [Part::Cone] Cone003
  Angle = 360
  Height = 1.5
  Placement = pos=(-30,-2,20) rot=(1,0,0;1.5708rad)
  Radius1 = 2.5
  Radius2 = 4
FEATURE [Part::Cone] Cone005
  Angle = 360
  Height = 1.5
  Placement = pos=(-31.9,-5,0) rot=(1,0,0;1.5708rad)
  Radius1 = 2.5
  Radius2 = 4
FEATURE [Part::Cone] Cone006
  Angle = 360
  Height = 1.5
  Placement = pos=(-30,-5,20) rot=(1,0,0;1.5708rad)
  Radius1 = 2.5
  Radius2 = 4
FEATURE [Part::Mirroring] Part__Mirroring002  label="Cone006 (Mirror #3)"
  Base = (0,0,0)
  Normal = (0,1,0)
  Placement = pos=(0,-3,0) rot=(0,0,1;0rad)
  Source = -> Cone006
FEATURE [Part::Box] Box112015002015  label="Cube080"
  Height = 14
  Length = 22
  Placement = pos=(-30,-3.5,13) rot=(0,0,1;0rad)
  Width = 7
FEATURE [Part::Box] Box112015002016  label="Cube081"
  Height = 16
  Length = 22
  Placement = pos=(-31.9,-3.5,-8) rot=(0,0,1;0rad)
  Width = 7
FEATURE [Part::Fuse] Fusion050
  Base = -> Cylinder054005
  Tool = -> Box112015002015
FEATURE [Part::Cut] Cut149
  Base = -> Fusion050
  Tool = -> Part__Mirroring002
FEATURE [Part::Cut] Cut150
  Base = -> Cut149
  Tool = -> Cone003
FEATURE [Part::Mirroring] Part__Mirroring003  label="Cone005 (Mirror #4)"
  Base = (0,0,0)
  Normal = (0,1,0)
  Placement = pos=(0,-3,0) rot=(0,0,1;0rad)
  Source = -> Cone005
FEATURE [Part::Cone] Cone007
  Angle = 360
  Height = 1.5
  Placement = pos=(-31.9,-2,0) rot=(1,0,0;1.5708rad)
  Radius1 = 2.5
  Radius2 = 4
FEATURE [Part::Fuse] Fusion051003
  Base = -> Cylinder054003
  Tool = -> Box112015002016
FEATURE [Part::Cut] Cut151
  Base = -> Fusion051003
  Tool = -> Cone007
FEATURE [Part::Cut] Cut152
  Base = -> Cut151
  Tool = -> Part__Mirroring003
FEATURE [Part::Cylinder] Cylinder054007
  Angle = 360
  Height = 56
  Placement = pos=(0,0,-8) rot=(0,0,1;0rad)
  Radius = 43
FEATURE [Part::Box] Box112015002017  label="Cube082"
  Height = 70
  Length = 40
  Placement = pos=(25,-50,-11) rot=(0,0,1;0rad)
  Width = 100
FEATURE [Part::Feature] Box112015002017001
  Placement = pos=(30.8013,46.6506,-11) rot=(0,0,1;2.0944rad)
  shape: bbox 106.6 x 84.64 x 70 mm, 6 faces (baked)
FEATURE [Part::Feature] Box112015002017002
  Placement = pos=(-55.8013,3.34936,-11) rot=(0,0,1;4.18879rad)
  shape: bbox 106.6 x 84.64 x 70 mm, 6 faces (baked)
FEATURE [Part::Cut] Cut153
  Base = -> Cylinder054007
  Tool = -> Box112015002017
FEATURE [Part::Cut] Cut154
  Base = -> Cut153
  Tool = -> Box112015002017002
FEATURE [Part::Cut] Cut155  label="carriage-blank"
  Base = -> Cut154
  Tool = -> Box112015002017001
FEATURE [Part::Box] Box112015002017003  label="Cube083"
  Height = 70
  Length = 40
  Placement = pos=(19,-20,-11) rot=(0,0,1;0rad)
  Width = 40
FEATURE [Part::Box] Box112015002017004  label="Cube084"
  Height = 70
  Length = 54
  Placement = pos=(-37,-50,-11) rot=(0,0,1;0rad)
  Width = 100
FEATURE [Part::Feature] Box112015002017004001
  Placement = pos=(61.8013,-7.04294,-11) rot=(0,0,1;2.0944rad)
  shape: bbox 113.6 x 96.77 x 70 mm, 6 faces (baked)
FEATURE [Part::Feature] Box112015002017004002
  Placement = pos=(-24.8013,57.0429,-11) rot=(0,0,1;4.18879rad)
  shape: bbox 113.6 x 96.77 x 70 mm, 6 faces (baked)
FEATURE [Part::MultiCommon] Common008
  Shapes = -> [Box112015002017004,Box112015002017004001]
FEATURE [Part::MultiCommon] Common009
  Shapes = -> [Common008,Box112015002017004002]
FEATURE [Part::Chamfer] Chamfer
  Base = -> Common009
  Edges = 1 edges r=9: [Edge6]
FEATURE [Part::Chamfer] Chamfer001
  Base = -> Chamfer
  Edges = 1 edges r=9: [Edge6]
FEATURE [Part::Chamfer] Chamfer002  label="inner-void"
  Base = -> Chamfer001
  Edges = 1 edges r=9: [Edge13]
FEATURE [Part::Box] Box112015002017004003  label="V-case-cut"
  Height = 50
  Length = 50
  Placement = pos=(-99,-20,20) rot=(0,1,0;0.785398rad)
  Width = 40
FEATURE [Part::Box] Box112015002017004004  label="Cube086"
  Height = 50
  Length = 50
  Placement = pos=(-99,-20,20) rot=(0,1,0;0.785398rad)
  Width = 40
FEATURE [Part::Cylinder] Cylinder054008  label="v-bearing-1-m004"
  Angle = 360
  Height = 20
  Placement = pos=(-31.9,29,0) rot=(1,0,0;1.5708rad)
  Radius = 4
FEATURE [Part::Box] Box112015002017004005  label="Cube087"
  Height = 29
  Length = 19
  Placement = pos=(-47,-15,-15) rot=(0,0,1;0rad)
  Width = 30
FEATURE [Part::Chamfer] Chamfer005
  Base = -> Box112015002017004005
  Edges = 1 edges r=15: [Edge6]
  Placement = pos=(0,0,6) rot=(0,0,1;0rad)
FEATURE [Part::Mirroring] Part__Mirroring005  label="Chamfer005 (Mirror #6)"
  Base = (0,0,20)
  Normal = (0,0,1)
  Source = -> Chamfer005
FEATURE [Part::Chamfer] Chamfer006
  Base = -> Box112015002017004005
  Edges = 1 edges r=15: [Edge6]
  Placement = pos=(0,0,6) rot=(0,0,1;0rad)
FEATURE [Part::Feature] Part__Mirroring005001
  Placement = pos=(0,0,0) rot=(0,0,1;2.0944rad)
  shape: bbox 35.48 x 31.45 x 29 mm, 7 faces (baked)
FEATURE [Part::Feature] Part__Mirroring005002
  Placement = pos=(0,0,0) rot=(0,0,1;4.18879rad)
  shape: bbox 35.48 x 31.45 x 29 mm, 7 faces (baked)
FEATURE [Part::Feature] Chamfer006001
  Placement = pos=(0,0,6) rot=(0,0,1;2.0944rad)
  shape: bbox 35.48 x 31.45 x 29 mm, 7 faces (baked)
FEATURE [Part::Feature] Chamfer006002
  Placement = pos=(0,0,6) rot=(0,0,1;4.18879rad)
  shape: bbox 35.48 x 31.45 x 29 mm, 7 faces (baked)
FEATURE [Part::Feature] Cylinder054010  label="PTFE-tube-1"
  Placement = pos=(11.5,-19.9186,-5) rot=(0,0,1;2.0944rad)
  shape: bbox 4 x 4 x 110 mm, 3 faces (baked)
FEATURE [Part::Feature] Cylinder054011  label="PTFE-tube-2"
  Placement = pos=(11.5,19.9186,-5) rot=(0,0,1;4.18879rad)
  shape: bbox 4 x 4 x 110 mm, 3 faces (baked)
FEATURE [Part::Box] Box112015002017004006  label="section-intersector"
  Height = 23
  Length = 100
  Placement = pos=(-50,-50,66) rot=(0,0,1;0rad)
  Width = 100
FEATURE [Part::Chamfer] Chamfer006009
  Base = -> Cut144
  Edges = 1 edges r=1: [Edge1]
FEATURE [Part::Chamfer] Chamfer006010  label="locating-cylinder"
  Base = -> Chamfer006009
  Edges = 1 edges r=0.6: [Edge3]
FEATURE [Part::Cylinder] Cylinder054012
  Angle = 360
  Height = 20
  Placement = pos=(-30,27,20) rot=(1,0,0;1.5708rad)
  Radius = 4
FEATURE [Part::Box] Box112015002017004007  label="Cube088"
  Height = 70
  Length = 40
  Placement = pos=(20,-20,-15) rot=(0,0,1;0rad)
  Width = 40
FEATURE [Part::Feature] Box112015002017004007001
  Placement = pos=(56.8205,-58.416,0) rot=(0,0,1;2.0944rad)
  shape: bbox 54.64 x 54.64 x 40 mm, 6 faces (baked)
FEATURE [Part::Feature] Box112015002017004007002
  Placement = pos=(22.1795,78.416,0) rot=(0,0,1;4.18879rad)
  shape: bbox 54.64 x 54.64 x 40 mm, 6 faces (baked)
FEATURE [Part::Chamfer] Chamfer006011
  Base = -> Box112015002017004007
  Edges = 1 edges r=6: [Edge1]
FEATURE [Part::Chamfer] Chamfer006012  label="side-chop-3"
  Base = -> Chamfer006011
  Edges = 1 edges r=6: [Edge3]
FEATURE [Part::Feature] Chamfer006012001  label="side-chop-1"
  Placement = pos=(0,0,0) rot=(0,0,1;2.0944rad)
  shape: bbox 51.64 x 51.64 x 70 mm, 8 faces (baked)
FEATURE [Part::Feature] Chamfer006012002  label="side-chop-2"
  Placement = pos=(0,0,0) rot=(0,0,1;4.18879rad)
  shape: bbox 51.64 x 51.64 x 70 mm, 8 faces (baked)
FEATURE [Part::Sphere] Sphere
  Angle1 = -90
  Angle2 = 90
  Angle3 = 360
  Placement = pos=(0,0,6) rot=(0,0,1;0rad)
  Radius = 3
FEATURE [Part::Box] Box112015002017004007003  label="Cube089"
  Height = 8
  Length = 56
  Placement = pos=(-5,-5,0) rot=(0,0,1;0rad)
  Width = 46
FEATURE [Part::Feature] Sphere001 .. Sphere005  x5 (patterned run collapsed; names and placements below)
  shape: bbox 6 x 6 x 6 mm, 1 faces (baked)
  placements: 5 in arithmetic series — first pos=(9,0,6.3) rot=(0,0,1;0rad), step (9,0,0.3), last pos=(45,0,7.5) rot=(0,0,1;0rad)
FEATURE [Part::Sphere] Sphere006
  Angle1 = -90
  Angle2 = 90
  Angle3 = 360
  Placement = pos=(0,9,6) rot=(0,0,1;0rad)
  Radius = 3.1
FEATURE [Part::Feature] Sphere006001 .. Sphere006005  x5 (patterned run collapsed; names and placements below)
  shape: bbox 6.2 x 6.2 x 6.2 mm, 1 faces (baked)
  placements: 5 in arithmetic series — first pos=(9,9,6.3) rot=(0,0,1;0rad), step (9,0,0.3), last pos=(45,9,7.5) rot=(0,0,1;0rad)
FEATURE [Part::Sphere] Sphere006006
  Angle1 = -90
  Angle2 = 90
  Angle3 = 360
  Placement = pos=(0,18,6) rot=(0,0,1;0rad)
  Radius = 3.2
FEATURE [Part::Feature] Sphere006006001 .. Sphere006006005  x5 (patterned run collapsed; names and placements below)
  shape: bbox 6.4 x 6.4 x 6.4 mm, 1 faces (baked)
  placements: 5 in arithmetic series — first pos=(9,18,6.3) rot=(0,0,1;0rad), step (9,0,0.3), last pos=(45,18,7.5) rot=(0,0,1;0rad)
FEATURE [Part::Sphere] Sphere006006006
  Angle1 = -90
  Angle2 = 90
  Angle3 = 360
  Placement = pos=(0,27,6) rot=(0,0,1;0rad)
  Radius = 3.3
FEATURE [Part::Feature] Sphere006006006001 .. Sphere006006006005  x5 (patterned run collapsed; names and placements below)
  shape: bbox 6.6 x 6.6 x 6.6 mm, 1 faces (baked)
  placements: 5 in arithmetic series — first pos=(9,27,6.3) rot=(0,0,1;0rad), step (9,0,0.3), last pos=(45,27,7.5) rot=(0,0,1;0rad)
FEATURE [Part::Sphere] Sphere006006006006
  Angle1 = -90
  Angle2 = 90
  Angle3 = 360
  Placement = pos=(0,36,6) rot=(0,0,1;0rad)
  Radius = 3.4
FEATURE [Part::Feature] Sphere006006006006001 .. Sphere006006006006005  x5 (patterned run collapsed; names and placements below)
  shape: bbox 6.8 x 6.8 x 6.8 mm, 1 faces (baked)
  placements: 5 in arithmetic series — first pos=(9,36,6.3) rot=(0,0,1;0rad), step (9,0,0.3), last pos=(45,36,7.5) rot=(0,0,1;0rad)
FEATURE [Part::Cut] Cut175
  Base = -> Box112015002017004007003
  Tool = -> Sphere
FEATURE [Part::Cut] Cut176
  Base = -> Cut175
  Tool = -> Sphere006006006006005
FEATURE [Part::Cut] Cut177
  Base = -> Cut176
  Tool = -> Sphere006006006006004
FEATURE [Part::Cut] Cut178
  Base = -> Cut177
  Tool = -> Sphere006006006006003
FEATURE [Part::Cut] Cut179
  Base = -> Cut178
  Tool = -> Sphere006006006006002
FEATURE [Part::Cut] Cut180
  Base = -> Cut179
  Tool = -> Sphere006006006006001
FEATURE [Part::Cut] Cut181
  Base = -> Cut180
  Tool = -> Sphere006006006006
FEATURE [Part::Cut] Cut182
  Base = -> Cut181
  Tool = -> Sphere006006006005
FEATURE [Part::Cut] Cut183
  Base = -> Cut182
  Tool = -> Sphere006006006004
FEATURE [Part::Cut] Cut184
  Base = -> Cut183
  Tool = -> Sphere006006006003
FEATURE [Part::Cut] Cut185
  Base = -> Cut184
  Tool = -> Sphere006006006002
FEATURE [Part::Cut] Cut186
  Base = -> Cut185
  Tool = -> Sphere006006006001
FEATURE [Part::Cut] Cut187
  Base = -> Cut186
  Tool = -> Sphere006006006
FEATURE [Part::Cut] Cut188
  Base = -> Cut187
  Tool = -> Sphere006006005
FEATURE [Part::Cut] Cut189
  Base = -> Cut188
  Tool = -> Sphere006006004
FEATURE [Part::Cut] Cut190
  Base = -> Cut189
  Tool = -> Sphere006006003
FEATURE [Part::Cut] Cut191
  Base = -> Cut190
  Tool = -> Sphere006006002
FEATURE [Part::Cut] Cut192
  Base = -> Cut191
  Tool = -> Sphere006006001
FEATURE [Part::Cut] Cut193
  Base = -> Cut192
  Tool = -> Sphere006006
FEATURE [Part::Cut] Cut194
  Base = -> Cut193
  Tool = -> Sphere006005
FEATURE [Part::Cut] Cut195
  Base = -> Cut194
  Tool = -> Sphere006004
FEATURE [Part::Cut] Cut196
  Base = -> Cut195
  Tool = -> Sphere006003
FEATURE [Part::Cut] Cut197
  Base = -> Cut196
  Tool = -> Sphere006002
FEATURE [Part::Cut] Cut198
  Base = -> Cut197
  Tool = -> Sphere006001
FEATURE [Part::Cut] Cut199
  Base = -> Cut198
  Tool = -> Sphere006
FEATURE [Part::Cut] Cut200
  Base = -> Cut199
  Tool = -> Sphere005
FEATURE [Part::Cut] Cut201
  Base = -> Cut200
  Tool = -> Sphere004
FEATURE [Part::Cut] Cut202
  Base = -> Cut201
  Tool = -> Sphere003
FEATURE [Part::Cut] Cut203
  Base = -> Cut202
  Tool = -> Sphere002
FEATURE [Part::Cut] Cut204
  Base = -> Cut203
  Tool = -> Sphere001
FEATURE [Part::Chamfer] Chamfer006012003  label="ball-socket-test"
  Base = -> Cut204
  Edges = 1 edges r=2: [Edge1]
FEATURE [App::DocumentObjectGroup] Group002  label="Experiments"
  Group = -> [Chamfer006012003]
FEATURE [Part::Cylinder] Cylinder054014  label="Cylinder054017"
  Angle = 360
  Height = 81
  Placement = pos=(0,0,-1) rot=(0,0,1;0rad)
  Radius = 1.7
FEATURE [Part::Cylinder] Cylinder054015  label="Cylinder054034"
  Angle = 360
  Height = 30
  Placement = pos=(0,0,-30) rot=(0,0,1;0rad)
  Radius = 5
FEATURE [Part::Box] Box112015002017004007004  label="Cube090"
  Height = 33
  Length = 12
  Placement = pos=(-6,2.75,-32) rot=(0,0,1;0rad)
  Width = 10
FEATURE [Part::Feature] Box112015002017004007004001
  Placement = pos=(-5.38157,-3.82115,-32) rot=(0,0,1;1.0472rad)
  shape: bbox 14.66 x 15.39 x 33 mm, 6 faces (baked)
FEATURE [Part::Feature] Box112015002017004007004002
  Placement = pos=(0.61843,-6.57115,-32) rot=(0,0,1;2.0944rad)
  shape: bbox 14.66 x 15.39 x 33 mm, 6 faces (baked)
FEATURE [Part::Feature] Box112015002017004007004003
  Placement = pos=(6,-2.75,-32) rot=(0,0,1;3.14159rad)
  shape: bbox 12 x 10 x 33 mm, 6 faces (baked)
FEATURE [Part::Feature] Box112015002017004007004004
  Placement = pos=(5.38157,3.82115,-32) rot=(0,0,1;4.18879rad)
  shape: bbox 14.66 x 15.39 x 33 mm, 6 faces (baked)
FEATURE [Part::Feature] Box112015002017004007004005
  Placement = pos=(-0.61843,6.57115,-32) rot=(0,0,-1;1.0472rad)
  shape: bbox 14.66 x 15.39 x 33 mm, 6 faces (baked)
FEATURE [Part::Cut] Cut205
  Base = -> Cylinder054015
  Tool = -> Box112015002017004007004
FEATURE [Part::Cut] Cut206
  Base = -> Cut205
  Tool = -> Box112015002017004007004005
FEATURE [Part::Cut] Cut207
  Base = -> Cut206
  Tool = -> Box112015002017004007004004
FEATURE [Part::Cut] Cut208
  Base = -> Cut207
  Tool = -> Box112015002017004007004003
FEATURE [Part::Cut] Cut209
  Base = -> Cut208
  Tool = -> Box112015002017004007004002
FEATURE [Part::Cut] Cut210
  Base = -> Cut209
  Tool = -> Box112015002017004007004001
FEATURE [Part::Fuse] Fusion051010003  label="M3-trapped-nut"
  Base = -> Cylinder054014
  Placement = pos=(0,0,0) rot=(0,1,0;1.5708rad)
  Tool = -> Cut210
FEATURE [Part::Fuse] Fusion051010004  label="M3-trapped-nut001"
  Base = -> Cylinder054014
  Placement = pos=(5,0,24) rot=(0,1,0;1.5708rad)
  Tool = -> Cut210
FEATURE [App::DocumentObjectGroup] Group003  label="Simple"
  Group = -> [Cylinder019,Cylinder035,Cylinder039,Box104,Box105,Box112,Box112003,Box110,Box111,Box112015,Box112017,Box112019,Box112022,Box112015002,Cylinder054,Box112015002017004004,Box112015002017003,Box112015002017004005]
FEATURE [Part::Cut] Cut211
  Base = -> Cylinder048
  Tool = -> Box112015002008
FEATURE [Part::Cut] Cut212
  Base = -> Cut211
  Tool = -> Box112015002014
FEATURE [Part::Cut] Cut213
  Base = -> Cut212
  Tool = -> Box112015002013
FEATURE [Part::Cut] Cut214
  Base = -> Cut213
  Tool = -> Box112015002012
FEATURE [Part::Cut] Cut215
  Base = -> Cut214
  Tool = -> Box112015002011
FEATURE [Part::Cut] Cut216  label="body-0"
  Base = -> Cut215
  Tool = -> Box112015002009
FEATURE [Part::Cone] Cone008
  Angle = 360
  Height = 2.5
  Placement = pos=(7,0,15) rot=(0,0,1;0rad)
  Radius1 = 5
  Radius2 = 2.5
FEATURE [Part::Cone] Cone009
  Angle = 360
  Height = 2.5
  Placement = pos=(7,0,-1.5) rot=(0,0,1;0rad)
  Radius1 = 7
  Radius2 = 4.5
FEATURE [Part::Cone] Cone010
  Angle = 360
  Height = 2.5
  Placement = pos=(7,0,-1.5) rot=(0,0,1;0rad)
  Radius1 = 7
  Radius2 = 4.5
FEATURE [Part::Box] Box112015002017004007004006  label="Cube091"
  Height = 10
  Length = 10
  Placement = pos=(-31,-7,19) rot=(0,0,1;0rad)
  Width = 14
FEATURE [Part::Fuse] Fusion051010010005  label="M3-trapped-nut-1"
  Base = -> Fusion051010004
  Placement = pos=(0,0,52) rot=(0,0,1;0rad)
  Tool = -> Box112015002017004007004006
FEATURE [Part::Fuse] Fusion051010010006  label="M3-trapped-nut-002"
  Base = -> Fusion051010004
  Tool = -> Box112015002017004007004006
FEATURE [Part::Mirroring] Part__Mirroring005004  label="Cone009 (Mirror #7)"
  Base = (0,0,50)
  Normal = (0,0,1)
  Source = -> Cone009
FEATURE [Part::Mirroring] Part__Mirroring005005  label="Cone (Mirror #8)"
  Base = (0,0,50)
  Normal = (0,0,1)
  Source = -> Cone
FEATURE [Part::Fuse] Fusion051010010007
  Base = -> Cylinder049
  Tool = -> Cylinder051
FEATURE [Part::Fuse] Fusion051010010008
  Base = -> Cylinder050
  Tool = -> Fusion051010010007
FEATURE [Part::Fuse] Fusion051010010009
  Base = -> Cone008
  Tool = -> Fusion051010010008
FEATURE [Part::Fuse] Fusion051010010010
  Base = -> Part__Mirroring005005
  Tool = -> Fusion051010010009
FEATURE [Part::Fuse] Fusion051010010011
  Base = -> Part__Mirroring005004
  Tool = -> Fusion051010010010
FEATURE [Part::Fuse] Fusion051010010012  label="through-hole"
  Base = -> Cone010
  Placement = pos=(0,-12,0) rot=(0,0,1;0rad)
  Tool = -> Fusion051010010011
FEATURE [Part::Feature] Fusion051010010012001
  Placement = pos=(-1,1,0) rot=(0,0,1;2.0944rad)
  shape: bbox 14 x 14 x 130 mm, 13 faces (baked)
FEATURE [Part::Feature] Fusion051010010012002
  Placement = pos=(-1,-1,0) rot=(0,0,1;4.18879rad)
  shape: bbox 14 x 14 x 130 mm, 13 faces (baked)
FEATURE [Part::Cut] Cut217  label="body-rule"
  Base = -> Cut216
  Tool = -> Box112015002010
FEATURE [Part::Cut] Cut218
  Base = -> Cut217
  Tool = -> Fusion051010010012002
FEATURE [Part::Cut] Cut220
  Base = -> Cut218
  Tool = -> Fusion051010010012001
FEATURE [Part::Fuse] Fusion051010010012003  label="through-hole001"
  Base = -> Cone010
  Placement = pos=(0,-12,0) rot=(0,0,1;0rad)
  Tool = -> Fusion051010010011
FEATURE [Part::Fuse] Fusion051010010012004  label="through-hole002"
  Base = -> Cone010
  Placement = pos=(0,12,0) rot=(0,0,1;0rad)
  Tool = -> Fusion051010010011
FEATURE [Part::Cut] Cut221
  Base = -> Cut220
  Tool = -> Fusion051010010012004
FEATURE [Part::Cut] Cut222  label="body-through-holes"
  Base = -> Cut221
  Tool = -> Fusion051010010012
FEATURE [Part::Cut] Cut223
  Base = -> Cut222
  Tool = -> Cylinder054010
FEATURE [Part::Cut] Cut224  label="body-ptfe"
  Base = -> Cut223
  Tool = -> Cylinder054011
FEATURE [Part::Cut] Cut225
  Base = -> Cut224
  Tool = -> Fusion051010010006
FEATURE [Part::Cut] Cut226  label="body-rule-adjusters"
  Base = -> Cut225
  Tool = -> Fusion051010010005
FEATURE [Part::Chamfer] Chamfer006012004
  Base = -> Cut226
  Edges = 1 edges r=3: [Edge139]
FEATURE [Part::Chamfer] Chamfer006012005
  Base = -> Chamfer006012004
  Edges = 1 edges r=3: [Edge186]
FEATURE [Part::Chamfer] Chamfer006012006
  Base = -> Chamfer006012005
  Edges = 1 edges r=3: [Edge38]
FEATURE [Part::Chamfer] Chamfer006012007
  Base = -> Chamfer006012006
  Edges = 1 edges r=3: [Edge123]
FEATURE [Part::Chamfer] Chamfer006012008
  Base = -> Chamfer006012007
  Edges = 1 edges r=3: [Edge165]
FEATURE [Part::Chamfer] Chamfer006012009
  Base = -> Chamfer006012008
  Edges = 1 edges r=3: [Edge116]
FEATURE [Part::Chamfer] Chamfer006012010
  Base = -> Chamfer006012009
  Edges = 1 edges r=3: [Edge151]
FEATURE [Part::Chamfer] Chamfer006012011  label="body-1"
  Base = -> Chamfer006012010
  Edges = 1 edges r=3: [Edge196]
FEATURE [Part::Box] Box112015002017004007004007  label="Cube092"
  Height = 16
  Length = 16
  Placement = pos=(0,-30,0) rot=(0,0,1;0rad)
  Width = 60
FEATURE [Part::Box] Box112015002017004007004008  label="Cube093"
  Height = 20
  Length = 100
  Placement = pos=(-50,-50,-28) rot=(0,0,1;0rad)
  Width = 100
FEATURE [Part::Sphere] Sphere006006006006006
  Angle1 = -90
  Angle2 = 90
  Angle3 = 360
  Placement = pos=(8,25,1.2) rot=(0,0,1;0rad)
  Radius = 3.05
FEATURE [Part::Sphere] Sphere006006006006007
  Angle1 = -90
  Angle2 = 90
  Angle3 = 360
  Placement = pos=(8,-25,1.2) rot=(0,0,1;0rad)
  Radius = 3.05
FEATURE [Part::Cut] Cut227
  Base = -> Box112015002017004007004007
  Tool = -> Sphere006006006006006
FEATURE [Part::Cut] Cut228
  Base = -> Cut227
  Placement = pos=(-22,0,3) rot=(0,1,0;2.35619rad)
  Tool = -> Sphere006006006006007
FEATURE [Part::Cut] Cut229  label="socket-bar"
  Base = -> Cut228
  Tool = -> Box112015002017004007004008
FEATURE [Part::Cylinder] Cylinder054016  label="Cylinder054061"
  Angle = 360
  Height = 4
  Placement = pos=(21,2,0) rot=(1,0,0;1.5708rad)
  Radius = 5
FEATURE [Part::Box] Box112015002017004007004010  label="Cube095"
  Height = 17
  Length = 34
  Placement = pos=(-40,5,-8) rot=(0,0,1;0rad)
  Width = 14
FEATURE [Part::Cylinder] Cylinder054019  label="fat-wire-hole"
  Angle = 360
  Height = 100
  Placement = pos=(-28,-5,-24) rot=(0,0,1;0rad)
  Radius = 1.2
FEATURE [Part::Cylinder] Cylinder054020  label="Cylinder054062"
  Angle = 360
  Height = 100
  Placement = pos=(-17,15,-24) rot=(0,0,1;0rad)
  Radius = 1.5
FEATURE [Part::Chamfer] Chamfer006012013
  Base = -> Chamfer001
  Edges = 1 edges r=9: [Edge13]
FEATURE [Part::Cut] Cut232
  Base = -> Box112015002017004007004010
  Tool = -> Chamfer006012013
FEATURE [Part::Cut] Cut233
  Base = -> Cut232
  Tool = -> Cylinder054020
FEATURE [Part::Chamfer] Chamfer006012014
  Base = -> Cut233
  Edges = 1 edges r=1: [Edge2]
FEATURE [Part::Chamfer] Chamfer006012015
  Base = -> Chamfer006012014
  Edges = 1 edges r=2.3: [Edge3]
FEATURE [Part::Fuse] Fusion051010010012006  label="M3-trapped-nut-003"
  Base = -> Fusion051010004
  Placement = pos=(-32,21,-25) rot=(0,0,-1;1.5708rad)
  Tool = -> Box112015002017004007004006
FEATURE [Part::Cut] Cut234
  Base = -> Chamfer006012015
  Tool = -> Fusion051010010012006
FEATURE [Part::Fuse] Fusion051010010012007
  Base = -> Chamfer006002
  Tool = -> Box112015002017004007002
FEATURE [Part::Fuse] Fusion051010010012009  label="bearing-case-cut-1"
  Base = -> Part__Mirroring005002
  Tool = -> Fusion051010010012007
FEATURE [Part::Fuse] Fusion051010010012010
  Base = -> Chamfer006001
  Tool = -> Box112015002017004007001
FEATURE [Part::Fuse] Fusion051010010012011  label="bearing-case-cut-2"
  Base = -> Part__Mirroring005001
  Tool = -> Fusion051010010012010
FEATURE [Part::Cylinder] Cylinder054021  label="wire"
  Angle = 360
  Height = 100
  Placement = pos=(-28,5,-24) rot=(0,0,1;0rad)
  Radius = 0.5
FEATURE [Part::Fuse] Fusion051010010012012  label="M3-trapped-nut-004"
  Base = -> Fusion051010004
  Placement = pos=(-30,-12,-4) rot=(0,0,1;1.5708rad)
  Tool = -> Box112015002017004007004006
FEATURE [Part::Fuse] Fusion051010010012013  label="M3-trapped-nut-005"
  Base = -> Fusion051010004
  Placement = pos=(-31.9,-14,-24) rot=(0,0,1;1.5708rad)
  Tool = -> Box112015002017004007004006
FEATURE [Part::Fuse] Fusion051010010012014
  Base = -> Cylinder054012
  Tool = -> Fusion051010010012012
FEATURE [Part::Fuse] Fusion051010010012015  label="623-bearing-cavity-1"
  Base = -> Cut150
  Tool = -> Fusion051010010012014
FEATURE [Part::Feature] Fusion051010010012015001  label="623-bearing-cavity-2"
  Placement = pos=(0,0,0) rot=(0,0,1;2.0944rad)
  shape: bbox 104.8 x 65.53 x 14 mm, 34 faces (baked)
FEATURE [Part::Feature] Fusion051010010012015002  label="623-bearing-cavity-3"
  Placement = pos=(0,0,0) rot=(0,0,1;4.18879rad)
  shape: bbox 104.8 x 65.53 x 14 mm, 34 faces (baked)
FEATURE [Part::Fuse] Fusion051010010012015003
  Base = -> Cut152
  Tool = -> Fusion051010010012013
FEATURE [Part::Fuse] Fusion051010010012015004  label="V-bearing-cavity-1"
  Base = -> Cylinder054008
  Placement = pos=(0,0,-1) rot=(0,0,1;0rad)
  Tool = -> Fusion051010010012015003
FEATURE [Part::Box] Box112015002017004007004011  label="Cube096"
  Height = 56
  Length = 34
  Placement = pos=(-44,-11,-8) rot=(0,0,1;0rad)
  Width = 22
FEATURE [Part::Box] Box112015002017004007004012  label="wire-clamp-slot"
  Height = 100
  Length = 28
  Placement = pos=(-47,4.5,-16) rot=(0,0,1;0rad)
  Width = 1
FEATURE [Part::Fuse] Fusion051010010012015005  label="carriage-blank-2"
  Base = -> Cut155
  Tool = -> Box112015002017004007004011
FEATURE [Part::Fuse] Fusion051010010012015006  label="V-bearing-cavity-2"
  Base = -> Cylinder054008
  Placement = pos=(0,0,41) rot=(0,0,1;0rad)
  Tool = -> Fusion051010010012015003
FEATURE [Part::Box] Box112015002017004007004013  label="rule005"
  Height = 324
  Length = 25.5
  Placement = pos=(-30,-2,-10) rot=(0,0,1;0rad)
  Width = 4
FEATURE [Part::Fuse] Fusion051010010012015008  label="inner-void-1"
  Base = -> Chamfer002
  Tool = -> Box112015002017004007004013
FEATURE [Part::Cut] Cut235
  Base = -> Fusion051010010012015005
  Tool = -> Chamfer006012
FEATURE [Part::Cut] Cut236
  Base = -> Cut235
  Tool = -> Chamfer006012002
FEATURE [Part::Cut] Cut237  label="carriage-blank-5"
  Base = -> Cut236
  Tool = -> Chamfer006012001
FEATURE [Part::Fuse] Fusion051010010012015009  label="carriage-blank-6"
  Base = -> Cut229
  Tool = -> Cut237
FEATURE [Part::Cut] Cut238  label="carriage-1"
  Base = -> Fusion051010010012015009
  Tool = -> Fusion051010010012015008
FEATURE [Part::Cut] Cut239
  Base = -> Cut238
  Tool = -> Fusion051010010012009
FEATURE [Part::Cut] Cut240
  Base = -> Cut239
  Tool = -> Fusion051010010012011
FEATURE [Part::Cut] Cut241  label="carriage-2"
  Base = -> Cut240
  Tool = -> Box112015002017004003
FEATURE [Part::Cut] Cut242
  Base = -> Cut241
  Tool = -> Fusion051010010012015001
FEATURE [Part::Cut] Cut243
  Base = -> Cut242
  Tool = -> Fusion051010010012015002
FEATURE [Part::Cut] Cut244
  Base = -> Cut243
  Tool = -> Fusion051010010012015006
FEATURE [Part::Cut] Cut245  label="carriage-3"
  Base = -> Cut244
  Tool = -> Fusion051010010012015004
FEATURE [Part::Cut] Cut246
  Base = -> Cut245
  Tool = -> Cylinder054019
FEATURE [Part::Cylinder] Cylinder054022  label="wire001"
  Angle = 360
  Height = 100
  Placement = pos=(-28,5,-24) rot=(0,0,1;0rad)
  Radius = 0.7
FEATURE [Part::Cut] Cut247  label="carriage-4"
  Base = -> Cut246
  Tool = -> Cylinder054022
FEATURE [Part::Box] Box112015002017004007004014  label="Cube097"
  Height = 33
  Length = 5.5
  Placement = pos=(-37.75,6,0) rot=(0,0,1;0rad)
  Width = 2.5
FEATURE [Part::Cylinder] Cylinder054023  label="grub-1"
  Angle = 360
  Height = 10
  Placement = pos=(-28,14,7.2) rot=(1,0,0;1.5708rad)
  Radius = 1.7
FEATURE [Part::Cylinder] Cylinder054024  label="grub-2"
  Angle = 360
  Height = 10
  Placement = pos=(-28,14,32) rot=(1,0,0;1.5708rad)
  Radius = 1.7
FEATURE [Part::Box] Box112015002017004007004015  label="Cube098"
  Height = 50
  Length = 50
  Placement = pos=(-94.75,4,20) rot=(0,1,0;0.785398rad)
  Width = 9.5
FEATURE [Part::Chamfer] Chamfer006012016
  Base = -> Box112015002017004007004014
  Edges = 1 edges r=2.6: [Edge2]
FEATURE [Part::Chamfer] Chamfer006012017
  Base = -> Chamfer006012016
  Edges = 1 edges r=2.6: [Edge15]
  Placement = pos=(7,0,4) rot=(0,0,1;0rad)
FEATURE [Part::Fuse] Fusion051010010012015010
  Base = -> Box112015002017004007004015
  Tool = -> Chamfer006012017
FEATURE [Part::Fuse] Fusion051010010012015011
  Base = -> Cylinder054024
  Tool = -> Fusion051010010012015010
FEATURE [Part::Fuse] Fusion051010010012015012  label="wire-screw-cavity"
  Base = -> Cylinder054023
  Tool = -> Fusion051010010012015011
FEATURE [Part::Cut] Cut248  label="carriage-5"
  Base = -> Cut247
  Tool = -> Fusion051010010012015012
FEATURE [App::DocumentObjectGroup] Group001  label="Old"
  Group = -> [Cut056,Cut070,Cylinder021,Cylinder022,Cut111,Chamfer006012011,Cylinder054021,Cut248,Box,Cylinder,Cylinder001,Cylinder036,Cylinder037,Chamfer006010]
FEATURE [Part::Box] Box112015002017004007004016  label="Cube099"
  Height = 14
  Length = 4.4
  Placement = pos=(-2.2,-2,-4) rot=(0,0,1;0rad)
  Width = 4
FEATURE [Part::Chamfer] Chamfer006012018
  Base = -> Box112015002017004007004016
  Edges = 1 edges r=2: [Edge6]
FEATURE [Part::Chamfer] Chamfer006012019
  Base = -> Chamfer006012018
  Edges = 1 edges r=2: [Edge15]
  Placement = pos=(0,0,2) rot=(0,0,1;0rad)
FEATURE [Part::Chamfer] Chamfer003
  Base = -> Chamfer006012019
  Edges = 1 edges r=2: [Edge14]
FEATURE [Part::Chamfer] Chamfer010  label="PTFE-slot-1"
  Base = -> Chamfer003
  Edges = 1 edges r=2: [Edge16]
FEATURE [Part::Cylinder] Cylinder054025  label="PTFE"
  Angle = 360
  Height = 10
  Placement = pos=(0,-5.75,0) rot=(0,0,1;0rad)
  Radius = 2
FEATURE [Part::Cylinder] Cylinder054026  label="Cylinder054063"
  Angle = 360
  Height = 1
  Placement = pos=(0,-1.5,2) rot=(1,0,0;1.5708rad)
  Radius = 2
FEATURE [Part::Cylinder] Cylinder054027  label="Cylinder054064"
  Angle = 360
  Height = 1
  Placement = pos=(0,-1.5,8) rot=(1,0,0;1.5708rad)
  Radius = 2
FEATURE [Part::Chamfer] Chamfer006012020  label="PTFE-slot-002"
  Base = -> Chamfer003
  Edges = 1 edges r=2: [Edge16]
  Placement = pos=(0,-6.25,0) rot=(0,0,1;0rad)
FEATURE [Part::Fuse] Fusion051010010012015013
  Base = -> Chamfer010
  Tool = -> Cylinder054026
FEATURE [Part::Fuse] Fusion051010010012015014
  Base = -> Cylinder054027
  Placement = pos=(0,-6.25,0) rot=(0,0,1;0rad)
  Tool = -> Fusion051010010012015013
FEATURE [Part::Cylinder] Cylinder054028  label="steel"
  Angle = 360
  Height = 100
  Placement = pos=(0,0,-50) rot=(0,0,1;0rad)
  Radius = 4
FEATURE [Part::Feature] Fusion051010010012015014001  label="reactor-slot-1"
  Placement = pos=(5.41266,3.125,0) rot=(0,0,1;2.0944rad)
  shape: bbox 5.997 x 5.887 x 14 mm, 14 faces (baked)
FEATURE [Part::Feature] Fusion051010010012015014002  label="reactor-slot-2"
  Placement = pos=(-5.41266,3.125,0) rot=(0,0,1;4.18879rad)
  shape: bbox 5.997 x 5.887 x 14 mm, 14 faces (baked)
FEATURE [Part::Cylinder] Cylinder054029  label="M4-adjuster"
  Angle = 360
  Height = 20
  Placement = pos=(0,-5,5) rot=(1,0,0;1.5708rad)
  Radius = 1.7
FEATURE [Part::Fuse] Fusion051010010012015014003  label="adjuster-slot"
  Base = -> Chamfer006012020
  Tool = -> Cylinder054029
FEATURE [Part::Cylinder] Cylinder054031  label="steel002"
  Angle = 360
  Height = 200
  Placement = pos=(0,0,-100) rot=(0,0,1;0rad)
  Radius = 5
FEATURE [Part::Box] Box112015002017004007004017  label="Cube100"
  Height = 16
  Length = 16
  Placement = pos=(0,-30,0) rot=(0,0,1;0rad)
  Width = 60
FEATURE [Part::Box] Box112015002017004007004018  label="Cube101"
  Height = 20
  Length = 100
  Placement = pos=(-50,-50,-28) rot=(0,0,1;0rad)
  Width = 100
FEATURE [Part::Sphere] Sphere006006006006008
  Angle1 = -90
  Angle2 = 90
  Angle3 = 360
  Placement = pos=(8,25,1.2) rot=(0,0,1;0rad)
  Radius = 3.05
FEATURE [Part::Sphere] Sphere006006006006009
  Angle1 = -90
  Angle2 = 90
  Angle3 = 360
  Placement = pos=(8,-25,1.2) rot=(0,0,1;0rad)
  Radius = 3.05
FEATURE [Part::Cut] Cut253
  Base = -> Box112015002017004007004017
  Tool = -> Sphere006006006006008
FEATURE [Part::Cut] Cut254
  Base = -> Cut253
  Placement = pos=(-22,0,3) rot=(0,1,0;2.35619rad)
  Tool = -> Sphere006006006006009
FEATURE [Part::Cut] Cut255  label="socket-bar001"
  Base = -> Cut254
  Placement = pos=(22,0,-8) rot=(1,0,0;3.14159rad)
  Tool = -> Box112015002017004007004018
FEATURE [Part::Fuse] Fusion051010010012015014004
  Base = -> Fusion051010010012015014001
  Tool = -> Fusion051010010012015014002
FEATURE [Part::Fuse] Fusion051010010012015014005
  Base = -> Fusion051010010012015014003
  Tool = -> Fusion051010010012015014004
FEATURE [Part::Fuse] Fusion051010010012015014006  label="bearing-cavity-3a"
  Base = -> Cylinder054031
  Placement = pos=(9,-20,-4) rot=(0,1,0;3.14159rad)
  Tool = -> Fusion051010010012015014005
FEATURE [Part::Box] Box112015002017004007004019  label="Cube102"
  Height = 14
  Length = 4.4
  Placement = pos=(-2.2,-2,-4) rot=(0,0,1;0rad)
  Width = 4
FEATURE [Part::Chamfer] Chamfer006012021
  Base = -> Box112015002017004007004019
  Edges = 1 edges r=2: [Edge6]
FEATURE [Part::Chamfer] Chamfer006012022
  Base = -> Chamfer006012021
  Edges = 1 edges r=2: [Edge15]
  Placement = pos=(0,0,2) rot=(0,0,1;0rad)
FEATURE [Part::Chamfer] Chamfer006012023
  Base = -> Chamfer006012022
  Edges = 1 edges r=2: [Edge14]
FEATURE [Part::Chamfer] Chamfer006012024  label="PTFE-slot-003"
  Base = -> Chamfer006012023
  Edges = 1 edges r=2: [Edge16]
  Placement = pos=(0,-6.25,0) rot=(0,0,1;0rad)
FEATURE [Part::Cylinder] Cylinder054032  label="M4-adjuster001"
  Angle = 360
  Height = 20
  Placement = pos=(0,-5,5) rot=(1,0,0;1.5708rad)
  Radius = 1.7
FEATURE [Part::Fuse] Fusion051010010012015014007  label="adjuster-slot001"
  Base = -> Chamfer006012024
  Placement = pos=(-5,0,0) rot=(0,1,0;1.5708rad)
  Tool = -> Cylinder054032
FEATURE [Part::Feature] Fusion051010010012015014008  label="reactor-slot-003"
  Placement = pos=(-5,6.25,-6.13174e-07) rot=(0.707107,0,0.707107;3.14159rad)
  shape: bbox 14 x 4.5 x 4.4 mm, 14 faces (baked)
FEATURE [Part::Box] Box112015002017004007004020  label="Cube103"
  Height = 200
  Length = 16
  Placement = pos=(-8,-5,-100) rot=(0,0,1;0rad)
  Width = 10
FEATURE [Part::Fuse] Fusion051010010012015014009
  Base = -> Fusion051010010012015014008
  Tool = -> Box112015002017004007004020
FEATURE [Part::Fuse] Fusion051010010012015014010  label="bearing-cavity-2a"
  Base = -> Fusion051010010012015014007
  Placement = pos=(9,20,-9) rot=(-0.707107,0.707107,0;3.14159rad)
  Tool = -> Fusion051010010012015014009
FEATURE [Part::Fuse] Fusion051010010012015014011  label="bearing-cavity-2"
  Base = -> Fusion051010010012015014007
  Tool = -> Fusion051010010012015014009
FEATURE [Part::Fuse] Fusion051010010012015014012  label="bearing-cavity-3"
  Base = -> Cylinder054031
  Placement = pos=(0,0,0) rot=(0,0,-1;1.5708rad)
  Tool = -> Fusion051010010012015014005
FEATURE [Part::Fuse] Fusion051010010012015014013  label="bearing-cavity-3a001"
  Base = -> Cylinder054031
  Placement = pos=(9,-20,-44) rot=(0,1,0;3.14159rad)
  Tool = -> Fusion051010010012015014005
FEATURE [Part::Box] Box112015002017004007004021  label="Cube104"
  Height = 60
  Length = 22
  Placement = pos=(-1,-30,0) rot=(0,0,1;0rad)
  Width = 60
FEATURE [Part::Box] Box112015002017004007004022  label="Cube105"
  Height = 60
  Length = 24
  Placement = pos=(-2,-50,15) rot=(0,0,1;0rad)
  Width = 60
FEATURE [Part::Box] Box112015002017004007004023  label="Cube106"
  Height = 60
  Length = 10
  Placement = pos=(4,24,0) rot=(0,0,1;0rad)
  Width = 10
FEATURE [Part::Fuse] Fusion051010010012015014014
  Base = -> Box112015002017004007004021
  Tool = -> Box112015002017004007004023
FEATURE [Part::Cut] Cut256
  Base = -> Fusion051010010012015014014
  Placement = pos=(0,0,0) rot=(1,0,0;3.14159rad)
  Tool = -> Box112015002017004007004022
FEATURE [Part::Cylinder] Cylinder054033  label="centreline"
  Angle = 360
  Height = 500
  Placement = pos=(0,0,-350) rot=(0,0,1;0rad)
  Radius = 0.1
FEATURE [Part::Box] Box112015002017004007004024  label="wire-clamp-slot001"
  Height = 30
  Length = 1
  Placement = pos=(-0.5,-6,-19) rot=(0,0,1;0rad)
  Width = 2
FEATURE [Part::Cylinder] Cylinder054035  label="wire-clamp-screw-hole-1"
  Angle = 360
  Height = 10
  Placement = pos=(-9.5,-5,-4) rot=(0,1,0;1.5708rad)
  Radius = 1.7
FEATURE [Part::Cylinder] Cylinder054036  label="wire-clamp-screw-hole-2"
  Angle = 360
  Height = 10
  Placement = pos=(-9.5,-5,-12) rot=(0,1,0;1.5708rad)
  Radius = 1.7
FEATURE [Part::Box] Box112015002017004007004025  label="Cube108"
  Height = 15
  Length = 6
  Placement = pos=(-6.5,-9,-15) rot=(0,0,1;0rad)
  Width = 18
FEATURE [Part::Box] Box112015002017004007004026  label="wire-slot"
  Height = 30
  Length = 8
  Placement = pos=(-4,4,-19) rot=(0,0,1;0rad)
  Width = 2
FEATURE [Part::Cylinder] Cylinder054037  label="steel-3"
  Angle = 360
  Height = 395
  Placement = pos=(9,-20,-300) rot=(0,0,1;0rad)
  Radius = 4
FEATURE [Part::Cylinder] Cylinder054038  label="steel-2"
  Angle = 360
  Height = 395
  Placement = pos=(9,20,-300) rot=(0,0,1;0rad)
  Radius = 4
FEATURE [Part::Box] Box112015002017004007004027  label="Cube110"
  Height = 42
  Length = 32
  Placement = pos=(-11,-30,-1) rot=(0,0,1;0rad)
  Width = 60
FEATURE [Part::Box] Box112015002017004007004028  label="Cube111"
  Height = 35
  Length = 35
  Placement = pos=(-45,-17.5,-299) rot=(0,0,1;0rad)
  Width = 35
FEATURE [Part::Cylinder] Cylinder054039  label="drive"
  Angle = 360
  Height = 18
  Placement = pos=(-45,-17.5,-299) rot=(0,0,1;0rad)
  Radius = 5
FEATURE [Part::Cylinder] Cylinder054040  label="boss"
  Angle = 360
  Height = 2
  Placement = pos=(-45,-17.5,-299) rot=(0,0,1;0rad)
  Radius = 11
FEATURE [Part::Cylinder] Cylinder054041  label="M3-1"
  Angle = 360
  Height = 50
  Placement = pos=(-45,-17.5,-299) rot=(0,0,1;0rad)
  Radius = 1.7
FEATURE [Part::Cylinder] Cylinder054042  label="M3-2"
  Angle = 360
  Height = 50
  Placement = pos=(-45,-17.5,-299) rot=(0,0,1;0rad)
  Radius = 1.7
FEATURE [Part::Cylinder] Cylinder054043  label="M3-3"
  Angle = 360
  Height = 50
  Placement = pos=(-45,-17.5,-299) rot=(0,0,1;0rad)
  Radius = 1.7
FEATURE [Part::Cylinder] Cylinder054044  label="M3-4"
  Angle = 360
  Height = 50
  Placement = pos=(-45,-17.5,-299) rot=(0,0,1;0rad)
  Radius = 1.7
FEATURE [App::DocumentObjectGroup] Group005  label="NEMA-14"
  Group = -> [Box112015002017004007004028,Cylinder054039,Cylinder054040,Cylinder054041,Cylinder054042,Cylinder054043,Cylinder054044]
FEATURE [Part::Cylinder] Cylinder054045  label="boss001"
  Angle = 360
  Height = 3
  Placement = pos=(-11,0,17.5) rot=(0,1,0;1.5708rad)
  Radius = 12
FEATURE [Part::Cut] Cut264
  Base = -> Box112015002017004007004027
  Tool = -> Cylinder054045
FEATURE [Part::Cylinder] Cylinder054046  label="M3-005"
  Angle = 360
  Height = 50
  Placement = pos=(-12,13,30.5) rot=(0,1,0;1.5708rad)
  Radius = 1.7
FEATURE [Part::Cylinder] Cylinder054047  label="M3-006"
  Angle = 360
  Height = 50
  Placement = pos=(-12,-13,4.5) rot=(0,1,0;1.5708rad)
  Radius = 1.7
FEATURE [Part::Cylinder] Cylinder054048  label="M3-007"
  Angle = 360
  Height = 50
  Placement = pos=(-12,13,4.5) rot=(0,1,0;1.5708rad)
  Radius = 1.7
FEATURE [Part::Cylinder] Cylinder054049  label="M3-008"
  Angle = 360
  Height = 50
  Placement = pos=(-12,-13,30.5) rot=(0,1,0;1.5708rad)
  Radius = 1.7
FEATURE [Part::Cut] Cut265
  Base = -> Cut264
  Tool = -> Cylinder054046
FEATURE [Part::Cut] Cut266
  Base = -> Cut265
  Tool = -> Cylinder054049
FEATURE [Part::Cut] Cut267
  Base = -> Cut266
  Tool = -> Cylinder054048
FEATURE [Part::Cut] Cut268
  Base = -> Cut267
  Tool = -> Cylinder054047
FEATURE [Part::Cylinder] Cylinder054050  label="drive001"
  Angle = 360
  Height = 40
  Placement = pos=(-9,0,17.5) rot=(0,1,0;1.5708rad)
  Radius = 8
FEATURE [Part::Cut] Cut269
  Base = -> Cut268
  Tool = -> Cylinder054050
FEATURE [Part::Box] Box112015002017004007004029  label="Cube112"
  Height = 50
  Length = 18
  Placement = pos=(-8,-10,9) rot=(0,0,1;0rad)
  Width = 20
FEATURE [Part::Cut] Cut270
  Base = -> Cut269
  Tool = -> Box112015002017004007004029
FEATURE [Part::Cylinder] Cylinder054051  label="grub-003"
  Angle = 360
  Height = 30
  Placement = pos=(-28,26,32) rot=(1,0,0;1.5708rad)
  Radius = 1.7
FEATURE [Part::Box] Box112015002017004007004030  label="Cube113"
  Height = 33
  Length = 5.3
  Placement = pos=(-30.65,6,29) rot=(0,0,1;0rad)
  Width = 2.5
FEATURE [Part::Fuse] Fusion051010010012015014017  label="nut-trap"
  Base = -> Cylinder054051
  Placement = pos=(43,5,5) rot=(0,0,1;0rad)
  Tool = -> Box112015002017004007004030
FEATURE [Part::Box] Box112015002017004007004031  label="Cube114"
  Height = 50
  Length = 15
  Placement = pos=(10,19.25,-4) rot=(0,0,1;0rad)
  Width = 1.5
FEATURE [Part::Fuse] Fusion051010010012015014018  label="rod-clamp"
  Base = -> Fusion051010010012015014017
  Tool = -> Box112015002017004007004031
FEATURE [Part::Cylinder] Cylinder054052  label="steel-004"
  Angle = 360
  Height = 395
  Placement = pos=(9,20,-300) rot=(0,0,1;0rad)
  Radius = 3.9
FEATURE [Part::Fuse] Fusion051010010012015014019  label="rod-and-clamp"
  Base = -> Fusion051010010012015014018
  Tool = -> Cylinder054052
FEATURE [Part::Fuse] Fusion051010010012015014020  label="rod-and-clamp001"
  Base = -> Fusion051010010012015014018
  Tool = -> Cylinder054052
FEATURE [Part::Mirroring] Part__Mirroring005006  label="rod-and-clamp (Mirror #7)"
  Base = (0,0,0)
  Normal = (0,1,0)
  Source = -> Fusion051010010012015014019
FEATURE [Part::Cut] Cut271
  Base = -> Cut270
  Tool = -> Fusion051010010012015014020
FEATURE [Part::Cut] Cut272  label="base-block-b"
  Base = -> Cut271
  Placement = pos=(0,0,-299) rot=(0,0,1;0rad)
  Tool = -> Part__Mirroring005006
FEATURE [Part::Box] Box112015002017004007004032  label="Cube115"
  Height = 15
  Length = 32
  Placement = pos=(-11,-30,26) rot=(0,0,1;0rad)
  Width = 60
FEATURE [Part::Cylinder] Cylinder054053  label="grub-004"
  Angle = 360
  Height = 30
  Placement = pos=(-28,31,32) rot=(1,0,0;1.5708rad)
  Radius = 1.7
FEATURE [Part::Box] Box112015002017004007004034  label="Cube117"
  Height = 33
  Length = 5.3
  Placement = pos=(-30.65,6,29) rot=(0,0,1;0rad)
  Width = 2.5
FEATURE [Part::Fuse] Fusion051010010012015014021  label="nut-trap001"
  Base = -> Cylinder054053
  Placement = pos=(43,7,5) rot=(0,0,1;0rad)
  Tool = -> Box112015002017004007004034
FEATURE [Part::Box] Box112015002017004007004035  label="Cube118"
  Height = 50
  Length = 15
  Placement = pos=(10,19.25,-4) rot=(0,0,1;0rad)
  Width = 1.5
FEATURE [Part::Fuse] Fusion051010010012015014022  label="rod-clamp001"
  Base = -> Fusion051010010012015014021
  Tool = -> Box112015002017004007004035
FEATURE [Part::Cylinder] Cylinder054054  label="steel-005"
  Angle = 360
  Height = 395
  Placement = pos=(9,20,-300) rot=(0,0,1;0rad)
  Radius = 3.9
FEATURE [Part::Fuse] Fusion051010010012015014023  label="rod-and-clamp002"
  Base = -> Fusion051010010012015014022
  Tool = -> Cylinder054054
FEATURE [Part::Fuse] Fusion051010010012015014024  label="rod-and-clamp003"
  Base = -> Fusion051010010012015014022
  Tool = -> Cylinder054054
FEATURE [Part::Mirroring] Part__Mirroring005007  label="rod-and-clamp (Mirror #7)001"
  Base = (0,0,0)
  Normal = (0,1,0)
  Source = -> Fusion051010010012015014023
FEATURE [Part::Cylinder] Cylinder054055  label="V-bearing"
  Angle = 360
  Height = 4
  Placement = pos=(-2,0,92) rot=(0,1,0;1.5708rad)
  Radius = 6
FEATURE [Part::Cone] Cone011
  Angle = 360
  Height = 3
  Placement = pos=(0,0,2) rot=(0,0,1;0rad)
  Radius1 = 2.5
  Radius2 = 5.5
FEATURE [Part::Mirroring] Part__Mirroring005008  label="Cone011 (Mirror #9)"
  Base = (0,0,0)
  Normal = (0,0,1)
  Placement = pos=(0.1,0,38) rot=(0,1,0;1.5708rad)
  Source = -> Cone011
FEATURE [Part::Cone] Cone012
  Angle = 360
  Height = 3
  Placement = pos=(1.9,0,38) rot=(0,1,0;1.5708rad)
  Radius1 = 2.5
  Radius2 = 5.5
FEATURE [Part::Box] Box112015002017004007004036  label="Cube119"
  Height = 8
  Length = 60
  Placement = pos=(-4,-7,68) rot=(0,1,0;1.5708rad)
  Width = 14
FEATURE [Part::Box] Box112015002017004007004037  label="Cube120"
  Height = 16
  Length = 10
  Placement = pos=(-8,-14,43) rot=(0,1,0;1.5708rad)
  Width = 28
FEATURE [Part::Cylinder] Cylinder054056  label="bearing-M3"
  Angle = 360
  Height = 40
  Placement = pos=(-20,0,38) rot=(0,1,0;1.5708rad)
  Radius = 1.4
FEATURE [Part::Cylinder] Cylinder054057  label="Cylinder054065"
  Angle = 360
  Height = 10
  Radius = 5
FEATURE [Part::Box] Box112015002017004007004038  label="Cube121"
  Height = 12
  Length = 10
  Placement = pos=(-5,2.75,-1) rot=(0,0,1;0rad)
  Width = 10
FEATURE [Part::Feature] Box112015002017004007004038001
  Placement = pos=(-4.88157,-2.95513,-1) rot=(0,0,1;1.0472rad)
  shape: bbox 13.66 x 13.66 x 12 mm, 6 faces (baked)
FEATURE [Part::Feature] Box112015002017004007004038002
  Placement = pos=(0.11843,-5.70513,-1) rot=(0,0,1;2.0944rad)
  shape: bbox 13.66 x 13.66 x 12 mm, 6 faces (baked)
FEATURE [Part::Feature] Box112015002017004007004038003
  Placement = pos=(5,-2.75,-1) rot=(0,0,1;3.14159rad)
  shape: bbox 10 x 10 x 12 mm, 6 faces (baked)
FEATURE [Part::Feature] Box112015002017004007004038004
  Placement = pos=(4.88157,2.95513,-1) rot=(0,0,1;4.18879rad)
  shape: bbox 13.66 x 13.66 x 12 mm, 6 faces (baked)
FEATURE [Part::Feature] Box112015002017004007004038005
  Placement = pos=(-0.11843,5.70513,-1) rot=(0,0,-1;1.0472rad)
  shape: bbox 13.66 x 13.66 x 12 mm, 6 faces (baked)
FEATURE [Part::Cut] Cut273
  Base = -> Cylinder054057
  Tool = -> Box112015002017004007004038
FEATURE [Part::Cut] Cut274
  Base = -> Cut273
  Tool = -> Box112015002017004007004038005
FEATURE [Part::Cut] Cut275
  Base = -> Cut274
  Tool = -> Box112015002017004007004038004
FEATURE [Part::Cut] Cut276
  Base = -> Cut275
  Tool = -> Box112015002017004007004038003
FEATURE [Part::Cut] Cut277
  Base = -> Cut276
  Tool = -> Box112015002017004007004038002
FEATURE [Part::Cut] Cut278
  Base = -> Cut277
  Tool = -> Box112015002017004007004038001
FEATURE [Part::Cylinder] Cylinder054058  label="Cylinder054066"
  Angle = 360
  Height = 50
  Placement = pos=(0,0,-20) rot=(0,0,1;0rad)
  Radius = 1.7
FEATURE [Part::Fuse] Fusion051010010012015014025  label="M3-nut-hole"
  Base = -> Cut278
  Placement = pos=(0,-10.5,27) rot=(0,0,1;0rad)
  Tool = -> Cylinder054058
FEATURE [App::DocumentObjectGroup] Group004  label="Temporary"
  Group = -> [Fusion051010010012015014025]
FEATURE [Part::Box] Box112015002017004007004038006  label="Cube122"
  Height = 18
  Length = 10
  Placement = pos=(-9,-15,42) rot=(0,1,0;1.5708rad)
  Width = 30
FEATURE [Part::Box] Box112015002017004007004038007  label="Cube123"
  Height = 8
  Length = 60
  Placement = pos=(-4,-7,68) rot=(0,1,0;1.5708rad)
  Width = 14
FEATURE [Part::Cylinder] Cylinder054059  label="Cylinder054067"
  Angle = 360
  Height = 20
  Placement = pos=(-10,11,32) rot=(0,1,0;1.5708rad)
  Radius = 2
FEATURE [Part::Fuse] Fusion051010010012015014027  label="bearing-cones"
  Base = -> Part__Mirroring005008
  Tool = -> Cone012
FEATURE [Part::Box] Box112015002017004007004038008  label="Cube124"
  Height = 16
  Length = 10
  Placement = pos=(-8,-14,43) rot=(0,1,0;1.5708rad)
  Width = 28
FEATURE [Part::MultiCommon] Common010  label="bearing-cones-truncated"
  Shapes = -> [Box112015002017004007004038008,Fusion051010010012015014027]
FEATURE [Part::Fuse] Fusion051010010012015014029
  Base = -> Cut256
  Tool = -> Box112015002017004007004025
FEATURE [Part::Cut] Cut286
  Base = -> Fusion051010010012015014029
  Tool = -> Fusion051010010012015014013
FEATURE [Part::Cut] Cut287
  Base = -> Cut286
  Tool = -> Fusion051010010012015014006
FEATURE [Part::Cut] Cut288
  Base = -> Cut287
  Tool = -> Fusion051010010012015014010
FEATURE [Part::Cut] Cut289
  Base = -> Cut288
  Tool = -> Cylinder054036
FEATURE [Part::Cut] Cut290
  Base = -> Cut289
  Tool = -> Cylinder054035
FEATURE [Part::Cut] Cut291
  Base = -> Cut290
  Tool = -> Box112015002017004007004024
FEATURE [Part::Cut] Cut292  label="slider-blank"
  Base = -> Cut291
  Tool = -> Box112015002017004007004026
FEATURE [Part::Cut] Cut293  label="slider-blank001"
  Base = -> Cut291
  Tool = -> Box112015002017004007004026
FEATURE [Part::Box] Box112015002017004007004038009  label="Cube125"
  Height = 15
  Length = 31
  Placement = pos=(-15.5,-17,-13) rot=(0,0,1;0rad)
  Width = 34
FEATURE [Part::Box] Box112015002017004007004038010  label="Cube126"
  Height = 15
  Length = 31
  Placement = pos=(0.5,-35,-13) rot=(0,0,1;0rad)
  Width = 70
FEATURE [Part::Fuse] Fusion051010010012015014030
  Base = -> Box112015002017004007004038009
  Tool = -> Box112015002017004007004038010
FEATURE [Part::Cut] Cut294  label="ball-socket-tabs"
  Base = -> Cut255
  Tool = -> Fusion051010010012015014030
FEATURE [Part::Fuse] Fusion051010010012015014031  label="delta-slider"
  Base = -> Cut293
  Placement = pos=(0,0,-150) rot=(0,0,1;0rad)
  Tool = -> Cut294
FEATURE [Part::Cylinder] Cylinder054060  label="Cylinder054068"
  Angle = 360
  Height = 20
  Placement = pos=(-10,11,32) rot=(0,1,0;1.5708rad)
  Radius = 2.2
FEATURE [Part::Cylinder] Cylinder054061  label="Cylinder054069"
  Angle = 360
  Height = 50
  Placement = pos=(0,-10.5,7) rot=(0,0,1;0rad)
  Radius = 1.3
FEATURE [Part::Box] Box112015002017004007004038011  label="Cube127"
  Height = 20
  Length = 10
  Placement = pos=(18,-11,78) rot=(0,0,1;0rad)
  Width = 22
FEATURE [Part::Cylinder] Cylinder054062  label="Cylinder054070"
  Angle = 360
  Height = 30
  Placement = pos=(11,4.75,86) rot=(0,1,0;1.5708rad)
  Radius = 1.1
FEATURE [Part::Cylinder] Cylinder054063  label="Cylinder054071"
  Angle = 360
  Height = 30
  Placement = pos=(11,-4.75,86) rot=(0,1,0;1.5708rad)
  Radius = 1.1
FEATURE [Part::Fuse] Fusion051010010012015014032
  Base = -> Box112015002017004007004038011
  Tool = -> Cylinder054062
FEATURE [Part::Fuse] Fusion051010010012015014033  label="microswitch-cavity"
  Base = -> Cylinder054063
  Tool = -> Fusion051010010012015014032
FEATURE [Part::Chamfer] Chamfer006012025
  Base = -> Box112015002017004007004037
  Edges = 1 edges r=8: [Edge12]
FEATURE [Part::Chamfer] Chamfer006012026
  Base = -> Chamfer006012025
  Edges = 1 edges r=8: [Edge7]
FEATURE [Part::Cut] Cut298
  Base = -> Chamfer006012026
  Tool = -> Box112015002017004007004036
FEATURE [Part::Fuse] Fusion051010010012015014034
  Base = -> Common010
  Tool = -> Cut298
FEATURE [Part::Cut] Cut299
  Base = -> Fusion051010010012015014034
  Tool = -> Cylinder054056
FEATURE [Part::Cut] Cut300
  Base = -> Cut299
  Tool = -> Cylinder054060
FEATURE [Part::Cut] Cut301  label="wire-tensioner"
  Base = -> Cut300
  Placement = pos=(0,0,54) rot=(0,0,1;0rad)
  Tool = -> Cylinder054061
FEATURE [Part::Chamfer] Chamfer006012027
  Base = -> Box112015002017004007004038006
  Edges = 1 edges r=8: [Edge10]
FEATURE [Part::Chamfer] Chamfer006012028
  Base = -> Chamfer006012027
  Edges = 1 edges r=8: [Edge13]
FEATURE [Part::Cut] Cut302
  Base = -> Box112015002017004007004032
  Tool = -> Chamfer006012028
FEATURE [Part::Cut] Cut303
  Base = -> Cut302
  Tool = -> Box112015002017004007004038007
FEATURE [Part::Fuse] Fusion051010010012015014035
  Base = -> Cylinder054059
  Tool = -> Cut303
FEATURE [Part::Cut] Cut304
  Base = -> Fusion051010010012015014035
  Tool = -> Part__Mirroring005007
FEATURE [Part::Cut] Cut305
  Base = -> Cut304
  Placement = pos=(0,0,54) rot=(0,0,1;0rad)
  Tool = -> Fusion051010010012015014024
FEATURE [Part::Cut] Cut306  label="top-block-a"
  Base = -> Cut305
  Tool = -> Fusion051010010012015014033
FEATURE [Part::Cylinder] Cylinder054064  label="Cylinder054072"
  Angle = 360
  Height = 20
  Placement = pos=(20,-23,70) rot=(0,0,1;0rad)
  Radius = 18
FEATURE [Part::Cylinder] Cylinder054065  label="Cylinder054073"
  Angle = 360
  Height = 22
  Placement = pos=(20,-23,69) rot=(0,0,1;0rad)
  Radius = 16.7
FEATURE [Part::Cylinder] Cylinder054066  label="Cylinder054074"
  Angle = 360
  Height = 20
  Placement = pos=(6,-23,70) rot=(0,0,1;0rad)
  Radius = 4
FEATURE [Part::Cylinder] Cylinder054067  label="Cylinder054075"
  Angle = 360
  Height = 22
  Placement = pos=(6,-23,69) rot=(0,0,1;0rad)
  Radius = 2.7
FEATURE [Part::Cut] Cut307
  Base = -> Cylinder054064
  Tool = -> Cylinder054065
FEATURE [Part::Cut] Cut308
  Base = -> Cylinder054066
  Tool = -> Cylinder054067
FEATURE [Part::Box] Box112015002017004007004038012  label="Cube128"
  Height = 22
  Length = 39
  Placement = pos=(1,-23,69) rot=(0,0,1;0rad)
  Width = 24
FEATURE [Part::Box] Box112015002017004007004038013  label="Cube129"
  Height = 22
  Length = 39
  Placement = pos=(1,-23,69) rot=(0,0,1;0rad)
  Width = 24
FEATURE [Part::MultiCommon] Common011
  Shapes = -> [Cut307,Box112015002017004007004038012]
FEATURE [Part::Cut] Cut309
  Base = -> Cut308
  Tool = -> Box112015002017004007004038013
FEATURE [Part::Fuse] Fusion051010010012015014036  label="deep-curved-wire"
  Base = -> Common011
  Tool = -> Cut309
FEATURE [App::DocumentObjectGroup] Group  label="Construction"
  Group = -> [Fusion016,Common002,Cylinder047,Cylinder046,Cut130,Fillet002,Fusion042,Chamfer006,Part__Mirroring005,Group003,Fusion051010003,Fusion051010010012003,Box112015002017004006,Cylinder054016,Cut234,Fusion051010010012015,Box112015002017004007004012,Fusion051010010012015014011,Fusion051010010012015014012,Cylinder054033,Cylinder054025,Fusion051010010012015014,Cylinder054028,Fusion051010010012015014036]
FEATURE [Part::Cylinder] Cylinder054068  label="Cylinder054080"
  Angle = 360
  Height = 20
  Placement = pos=(20,-23,70) rot=(0,0,1;0rad)
  Radius = 18
FEATURE [Part::Cylinder] Cylinder054069  label="Cylinder054081"
  Angle = 360
  Height = 22
  Placement = pos=(20,-23,69) rot=(0,0,1;0rad)
  Radius = 16.7
FEATURE [Part::Cylinder] Cylinder054070  label="Cylinder054082"
  Angle = 360
  Height = 20
  Placement = pos=(6,-23,70) rot=(0,0,1;0rad)
  Radius = 4
FEATURE [Part::Cylinder] Cylinder054071  label="Cylinder054083"
  Angle = 360
  Height = 22
  Placement = pos=(6,-23,69) rot=(0,0,1;0rad)
  Radius = 2.7
FEATURE [Part::Cut] Cut310
  Base = -> Cylinder054068
  Tool = -> Cylinder054069
FEATURE [Part::Cut] Cut311
  Base = -> Cylinder054070
  Tool = -> Cylinder054071
FEATURE [Part::Box] Box112015002017004007004038014  label="Cube130"
  Height = 22
  Length = 39
  Placement = pos=(1,-23,69) rot=(0,0,1;0rad)
  Width = 24
FEATURE [Part::Box] Box112015002017004007004038015  label="Cube131"
  Height = 22
  Length = 39
  Placement = pos=(1,-23,69) rot=(0,0,1;0rad)
  Width = 24
FEATURE [Part::MultiCommon] Common012
  Shapes = -> [Cut310,Box112015002017004007004038014]
FEATURE [Part::Cut] Cut312
  Base = -> Cut311
  Tool = -> Box112015002017004007004038015
FEATURE [Part::Fuse] Fusion051010010012015014037  label="deep-wire001"
  Base = -> Common012
  Placement = pos=(0,0,3) rot=(0,0,1;0rad)
  Tool = -> Cut312
FEATURE [Part::Box] Box112015002017004007004038016  label="Cube132"
  Height = 22
  Length = 48
  Placement = pos=(-6,-35,86) rot=(0,-1,0;0.279253rad)
  Width = 40
FEATURE [Part::Box] Box112015002017004007004038017  label="Cube133"
  Height = 22
  Length = 48
  Placement = pos=(-6,-35,84) rot=(0,-1,0;0.279253rad)
  Width = 40
FEATURE [Part::MultiCommon] Common013
  Shapes = -> [Fusion051010010012015014037,Box112015002017004007004038017]
FEATURE [Part::Cut] Cut313  label="top-wire"
  Base = -> Common013
  Tool = -> Box112015002017004007004038016
FEATURE [Part::Cylinder] Cylinder054072  label="Cylinder054088"
  Angle = 360
  Height = 20
  Placement = pos=(20,-23,70) rot=(0,0,1;0rad)
  Radius = 18
FEATURE [Part::Cylinder] Cylinder054073  label="Cylinder054089"
  Angle = 360
  Height = 22
  Placement = pos=(20,-23,69) rot=(0,0,1;0rad)
  Radius = 16.7
FEATURE [Part::Cylinder] Cylinder054074  label="Cylinder054090"
  Angle = 360
  Height = 20
  Placement = pos=(6,-23,70) rot=(0,0,1;0rad)
  Radius = 4
FEATURE [Part::Cylinder] Cylinder054075  label="Cylinder054091"
  Angle = 360
  Height = 22
  Placement = pos=(6,-23,69) rot=(0,0,1;0rad)
  Radius = 2.7
FEATURE [Part::Cut] Cut314
  Base = -> Cylinder054072
  Tool = -> Cylinder054073
FEATURE [Part::Cut] Cut315
  Base = -> Cylinder054074
  Tool = -> Cylinder054075
FEATURE [Part::Box] Box112015002017004007004038018  label="Cube134"
  Height = 22
  Length = 39
  Placement = pos=(1,-23,69) rot=(0,0,1;0rad)
  Width = 24
FEATURE [Part::Box] Box112015002017004007004038019  label="Cube135"
  Height = 22
  Length = 39
  Placement = pos=(1,-23,69) rot=(0,0,1;0rad)
  Width = 24
FEATURE [Part::MultiCommon] Common014
  Shapes = -> [Cut314,Box112015002017004007004038018]
FEATURE [Part::Cut] Cut316
  Base = -> Cut315
  Tool = -> Box112015002017004007004038019
FEATURE [Part::Fuse] Fusion051010010012015014038  label="deep-wire002"
  Base = -> Common014
  Placement = pos=(0,0,3) rot=(0,0,1;0rad)
  Tool = -> Cut316
FEATURE [Part::Box] Box112015002017004007004038020  label="Cube136"
  Height = 22
  Length = 48
  Placement = pos=(-6,-35,86) rot=(0,-1,0;0.279253rad)
  Width = 40
FEATURE [Part::Box] Box112015002017004007004038021  label="Cube137"
  Height = 22
  Length = 48
  Placement = pos=(-6,-35,84) rot=(0,-1,0;0.279253rad)
  Width = 40
FEATURE [Part::MultiCommon] Common015
  Shapes = -> [Fusion051010010012015014038,Box112015002017004007004038021]
FEATURE [Part::Cut] Cut317  label="top-wire001"
  Base = -> Common015
  Tool = -> Box112015002017004007004038020
FEATURE [Part::Mirroring] Part__Mirroring005009  label="top-wire001 (Mirror #10)"
  Base = (0,0,0)
  Normal = (0,1,0)
  Source = -> Cut317
FEATURE [Part::Cut] Cut318
  Base = -> Cut306
  Tool = -> Cut313
FEATURE [Part::Cut] Cut319  label="top-block"
  Base = -> Cut318
  Tool = -> Part__Mirroring005009
FEATURE [Part::Cylinder] Cylinder054078  label="Cylinder054094"
  Angle = 360
  Height = 20
  Placement = pos=(6,-23,70) rot=(0,0,1;0rad)
  Radius = 4
FEATURE [Part::Cylinder] Cylinder054079  label="Cylinder054095"
  Angle = 360
  Height = 22
  Placement = pos=(6,-23,69) rot=(0,0,1;0rad)
  Radius = 2.7
FEATURE [Part::Cut] Cut321
  Base = -> Cylinder054078
  Tool = -> Cylinder054079
FEATURE [Part::Box] Box112015002017004007004038022  label="Cube138"
  Height = 22
  Length = 39
  Placement = pos=(6,-47,69) rot=(0,0,1;0rad)
  Width = 24
FEATURE [Part::MultiCommon] Common016
  Placement = pos=(0,0,-350) rot=(0,0,1;0rad)
  Shapes = -> [Cut321,Box112015002017004007004038022]
FEATURE [Part::Box] Box112015002017004007004038023  label="Cube139"
  Height = 20
  Length = 21
  Placement = pos=(-15,-27,-280) rot=(0,0,1;0rad)
  Width = 1.3
FEATURE [Part::Fuse] Fusion051010010012015014039  label="deep-straight-wire"
  Base = -> Common016
  Tool = -> Box112015002017004007004038023
FEATURE [Part::Box] Box112015002017004007004038024  label="Cube140"
  Height = 20
  Length = 29
  Placement = pos=(-17,-29,-282) rot=(0,0,1;0rad)
  Width = 13
FEATURE [Part::Box] Box112015002017004007004038025  label="Cube141"
  Height = 20
  Length = 29
  Placement = pos=(1,-29,-276) rot=(0,0,1;0rad)
  Width = 13
FEATURE [Part::Cut] Cut322
  Base = -> Fusion051010010012015014039
  Tool = -> Box112015002017004007004038024
FEATURE [Part::MultiCommon] Common017
  Placement = pos=(0,0,-36.5) rot=(0,0,1;0rad)
  Shapes = -> [Cut322,Box112015002017004007004038025]
FEATURE [Part::Box] Box112015002017004007004038026  label="Cube142"
  Height = 2
  Length = 29
  Placement = pos=(-28,-27,-298.5) rot=(0,0,1;0rad)
  Width = 2
FEATURE [Part::Box] Box112015002017004007004038027  label="Cube143"
  Height = 2
  Length = 29
  Placement = pos=(-28,-24.46,-298.5) rot=(0,0,1;0rad)
  Width = 2
FEATURE [Part::Cylinder] Cylinder054080  label="Cylinder054098"
  Angle = 360
  Height = 20
  Placement = pos=(6,-23,70) rot=(0,0,1;0rad)
  Radius = 4
FEATURE [Part::Cylinder] Cylinder054081  label="Cylinder054099"
  Angle = 360
  Height = 22
  Placement = pos=(6,-23,69) rot=(0,0,1;0rad)
  Radius = 2.7
FEATURE [Part::Cut] Cut323
  Base = -> Cylinder054080
  Tool = -> Cylinder054081
FEATURE [Part::Box] Box112015002017004007004038028  label="Cube144"
  Height = 22
  Length = 39
  Placement = pos=(6,-47,69) rot=(0,0,1;0rad)
  Width = 24
FEATURE [Part::MultiCommon] Common018
  Placement = pos=(0,0,-350) rot=(0,0,1;0rad)
  Shapes = -> [Cut323,Box112015002017004007004038028]
FEATURE [Part::Box] Box112015002017004007004038029  label="Cube145"
  Height = 20
  Length = 21
  Placement = pos=(-15,-27,-280) rot=(0,0,1;0rad)
  Width = 1.3
FEATURE [Part::Fuse] Fusion051010010012015014040  label="deep-straight-wire001"
  Base = -> Common018
  Tool = -> Box112015002017004007004038029
FEATURE [Part::Box] Box112015002017004007004038030  label="Cube146"
  Height = 20
  Length = 29
  Placement = pos=(-17,-29,-282) rot=(0,0,1;0rad)
  Width = 13
FEATURE [Part::Cut] Cut324
  Base = -> Fusion051010010012015014040
  Placement = pos=(-23,-14,-558.5) rot=(0.707107,-0.707107,0;3.14159rad)
  Tool = -> Box112015002017004007004038030
FEATURE [Part::Cylinder] Cylinder054082  label="Cylinder054102"
  Angle = 360
  Height = 20
  Placement = pos=(6,-23,70) rot=(0,0,1;0rad)
  Radius = 4
FEATURE [Part::Cylinder] Cylinder054083  label="Cylinder054103"
  Angle = 360
  Height = 22
  Placement = pos=(6,-23,69) rot=(0,0,1;0rad)
  Radius = 2.7
FEATURE [Part::Cut] Cut325
  Base = -> Cylinder054082
  Placement = pos=(0.7,47,-368.5) rot=(0,0,1;0rad)
  Tool = -> Cylinder054083
FEATURE [Part::Box] Box112015002017004007004038031  label="Cube147"
  Height = 20
  Length = 1.3
  Placement = pos=(2.7,-3,-298.5) rot=(0,0,1;0rad)
  Width = 27
FEATURE [Part::Box] Box112015002017004007004038032  label="Cube148"
  Height = 23
  Length = 24
  Placement = pos=(0,-7,-296.5) rot=(0,0,1;0rad)
  Width = 42
FEATURE [Part::Box] Box112015002017004007004038033  label="Cube149"
  Height = 23
  Length = 24
  Placement = pos=(-15,-18,-299.5) rot=(0,0,1;0rad)
  Width = 42
FEATURE [Part::Cut] Cut326
  Base = -> Cut325
  Tool = -> Box112015002017004007004038033
FEATURE [Part::Fuse] Fusion051010010012015014041
  Base = -> Box112015002017004007004038031
  Tool = -> Cut326
FEATURE [Part::Cut] Cut327
  Base = -> Fusion051010010012015014041
  Tool = -> Box112015002017004007004038032
FEATURE [Part::Fuse] Fusion051010010012015014042
  Base = -> Cut324
  Tool = -> Cut327
FEATURE [Part::Fuse] Fusion051010010012015014043  label="base-wire-1"
  Base = -> Box112015002017004007004038027
  Tool = -> Fusion051010010012015014042
FEATURE [Part::Fuse] Fusion051010010012015014044  label="base-wire-2"
  Base = -> Common017
  Tool = -> Box112015002017004007004038026
FEATURE [Part::Cut] Cut328
  Base = -> Cut272
  Tool = -> Fusion051010010012015014043
FEATURE [Part::Cut] Cut329  label="base-block"
  Base = -> Cut328
  Tool = -> Fusion051010010012015014044
